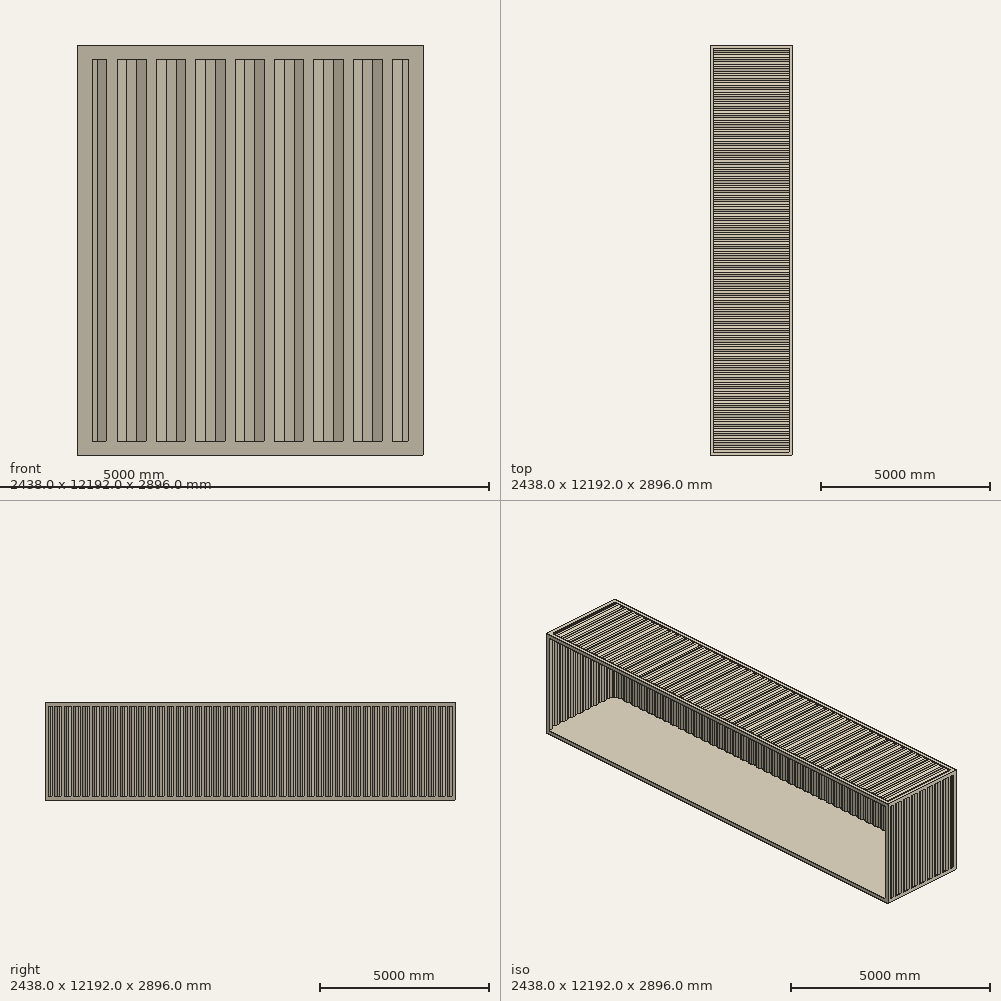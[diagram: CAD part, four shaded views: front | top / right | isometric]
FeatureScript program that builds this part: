
annotation { "Feature Type Name" : "Feature", "Feature Type Description" : "" }
export const myFeature = defineFeature(function(context is Context, id is Id, definition is map)
    precondition{}
    {
        {
            var Q0;
            Q0=qCreatedBy(makeId("Top.planeOp"),FACE);
            var sketch = newSketch(context, id + "F0", { "sketchPlane" : qUnion([Q0])});
            skLineSegment(sketch, "E0.bottom", {"start": v(0, 0) * mm, "end": v(-2438, 0) * mm});
            skLineSegment(sketch, "E0.top", {"start": v(0, 12192) * mm, "end": v(-2438, 12192) * mm});
            skLineSegment(sketch, "E0.left", {"start": v(0, 0) * mm, "end": v(0, 12192) * mm});
            skLineSegment(sketch, "E0.right", {"start": v(-2438, 0) * mm, "end": v(-2438, 12192) * mm});
            skSolve(sketch);
        }
        {
            var Q0;
            Q0=qSketchRegion(id+"F0",true);
            extrude(context, id + "F1", {"entities" : qUnion([Q0]), "depth" : 2896 * mm, "offsetDistance" : 25 * mm});
        }
        {
            var Q0;
            Q0=makeQuery(id+"F1.opExtrude","SWEPT_FACE",FACE,{"disambiguationData":[OSD([sQuery(id+"F0.wireOp",EDGE,"E0.bottom")])]});
            var sketch = newSketch(context, id + "F2", { "sketchPlane" : qUnion([Q0])});
            skLineSegment(sketch, "E1", {"start": v(-2438, 2896) * mm, "end": v(-2338, 2896) * mm});
            skLineSegment(sketch, "E2", {"start": v(-2338, 2896) * mm, "end": v(-2338, 100) * mm});
            skLineSegment(sketch, "E3", {"start": v(-2338, 100) * mm, "end": v(-100, 100) * mm});
            skLineSegment(sketch, "E4", {"start": v(-100, 100) * mm, "end": v(-100, 2796) * mm});
            skLineSegment(sketch, "E5", {"start": v(-100, 2796) * mm, "end": v(-2338, 2796) * mm});
            skSolve(sketch);
        }
        {
            var Q0;
            Q0=qSketchRegion(id+"F2",true);
            extrude(context, id + "F3", {"entities" : qUnion([Q0]), "operationType" : NewBodyOperationType.REMOVE, "oppositeDirection" : true, "depth" : 12192 * mm, "offsetDistance" : 25 * mm});
        }
        {
            var Q0;
            Q0=makeQuery(id+"F1.opExtrude","SWEPT_FACE",FACE,{"disambiguationData":[OSD([sQuery(id+"F0.wireOp",EDGE,"E0.left")])]});
            var sketch = newSketch(context, id + "F4", { "sketchPlane" : qUnion([Q0])});
            skLineSegment(sketch, "E6", {"start": v(0, 2896) * mm, "end": v(100, 2896) * mm});
            skLineSegment(sketch, "E7", {"start": v(100, 2896) * mm, "end": v(100, 100) * mm});
            skLineSegment(sketch, "E8", {"start": v(100, 100) * mm, "end": v(12092, 100) * mm});
            skLineSegment(sketch, "E9", {"start": v(12092, 100) * mm, "end": v(12092, 2796) * mm});
            skLineSegment(sketch, "E10", {"start": v(12092, 2796) * mm, "end": v(100, 2796) * mm});
            skSolve(sketch);
        }
        {
            var Q0;
            Q0=qSketchRegion(id+"F4",true);
            extrude(context, id + "F5", {"entities" : qUnion([Q0]), "operationType" : NewBodyOperationType.REMOVE, "oppositeDirection" : true, "depth" : 2438 * mm, "offsetDistance" : 25 * mm});
        }
        {
            var Q0;
            Q0=makeQuery(id+"F1.opExtrude","CAP_FACE",FACE,{"disambiguationData":[OSD([sQuery(id+"F0.wireOp",EDGE,"E0.bottom"),sQuery(id+"F0.wireOp",EDGE,"E0.top"),sQuery(id+"F0.wireOp",EDGE,"E0.left"),sQuery(id+"F0.wireOp",EDGE,"E0.right")])],"isStart":false});
            var sketch = newSketch(context, id + "F6", { "sketchPlane" : qUnion([Q0])});
            skLineSegment(sketch, "E11", {"start": v(-2438, 0) * mm, "end": v(-2338, 0) * mm});
            skLineSegment(sketch, "E12", {"start": v(-2338, 0) * mm, "end": v(-2338, 12092) * mm});
            skLineSegment(sketch, "E13", {"start": v(-2338, 12092) * mm, "end": v(-100, 12092) * mm});
            skLineSegment(sketch, "E14", {"start": v(-100, 12092) * mm, "end": v(-100, 100) * mm});
            skLineSegment(sketch, "E15", {"start": v(-100, 100) * mm, "end": v(-2338, 100) * mm});
            skSolve(sketch);
        }
        {
            var Q0;
            Q0=qSketchRegion(id+"F6",true);
            extrude(context, id + "F7", {"entities" : qUnion([Q0]), "operationType" : NewBodyOperationType.REMOVE, "oppositeDirection" : true, "depth" : 100 * mm, "offsetDistance" : 25 * mm});
        }
        {
            var Q0;
            Q0=makeQuery(id+"F5.boolean.opBoolean","MERGE",FACE,{"derivedFrom":[makeQuery(id+"F3.boolean.opBoolean","COPY",FACE,{"derivedFrom":makeQuery(id+"F3.opExtrude","SWEPT_FACE",FACE,{"disambiguationData":[OSD([sQuery(id+"F2.wireOp",EDGE,"E3")])]})})],"fromTools":[makeQuery(id+"F5.opExtrude","SWEPT_FACE",FACE,{"disambiguationData":[OSD([sQuery(id+"F4.wireOp",EDGE,"E8")])]})]});
            var sketch = newSketch(context, id + "F8", { "sketchPlane" : qUnion([Q0])});
            skLineSegment(sketch, "E16", {"start": v(-2338, 36) * mm, "end": v(-2301, 36) * mm});
            skLineSegment(sketch, "E17", {"start": v(-2233, 0) * mm, "end": v(-2161, 0) * mm});
            skLineSegment(sketch, "E18", {"start": v(-2093, 36) * mm, "end": v(-2023, 36) * mm});
            skLineSegment(sketch, "E19", {"start": v(-2301, 36) * mm, "end": v(-2233, 0) * mm});
            skLineSegment(sketch, "E20", {"start": v(-2161, 0) * mm, "end": v(-2093, 36) * mm});
            skLineSegment(sketch, "E21.1.0.0", {"start": v(-2023, 36) * mm, "end": v(-1955, 0) * mm});
            skLineSegment(sketch, "E21.1.0.1", {"start": v(-1955, 0) * mm, "end": v(-1883, 0) * mm});
            skLineSegment(sketch, "E21.1.0.2", {"start": v(-1883, 0) * mm, "end": v(-1815, 36) * mm});
            skLineSegment(sketch, "E21.1.0.3", {"start": v(-1815, 36) * mm, "end": v(-1745, 36) * mm});
            skLineSegment(sketch, "E21.2.0.0", {"start": v(-1745, 36) * mm, "end": v(-1677, 0) * mm});
            skLineSegment(sketch, "E21.2.0.1", {"start": v(-1677, 0) * mm, "end": v(-1605, 0) * mm});
            skLineSegment(sketch, "E21.2.0.2", {"start": v(-1605, 0) * mm, "end": v(-1537, 36) * mm});
            skLineSegment(sketch, "E21.2.0.3", {"start": v(-1537, 36) * mm, "end": v(-1467, 36) * mm});
            skLineSegment(sketch, "E21.3.0.0", {"start": v(-1467, 36) * mm, "end": v(-1399, 0) * mm});
            skLineSegment(sketch, "E21.3.0.1", {"start": v(-1399, 0) * mm, "end": v(-1327, 0) * mm});
            skLineSegment(sketch, "E21.3.0.2", {"start": v(-1327, 0) * mm, "end": v(-1259, 36) * mm});
            skLineSegment(sketch, "E21.3.0.3", {"start": v(-1259, 36) * mm, "end": v(-1189, 36) * mm});
            skLineSegment(sketch, "E21.4.0.0", {"start": v(-1189, 36) * mm, "end": v(-1121, 0) * mm});
            skLineSegment(sketch, "E21.4.0.1", {"start": v(-1121, 0) * mm, "end": v(-1049, 0) * mm});
            skLineSegment(sketch, "E21.4.0.2", {"start": v(-1049, 0) * mm, "end": v(-981, 36) * mm});
            skLineSegment(sketch, "E21.4.0.3", {"start": v(-981, 36) * mm, "end": v(-911, 36) * mm});
            skLineSegment(sketch, "E21.5.0.0", {"start": v(-911, 36) * mm, "end": v(-843, 0) * mm});
            skLineSegment(sketch, "E21.5.0.1", {"start": v(-843, 0) * mm, "end": v(-771, 0) * mm});
            skLineSegment(sketch, "E21.5.0.2", {"start": v(-771, 0) * mm, "end": v(-703, 36) * mm});
            skLineSegment(sketch, "E21.5.0.3", {"start": v(-703, 36) * mm, "end": v(-633, 36) * mm});
            skLineSegment(sketch, "E21.6.0.0", {"start": v(-633, 36) * mm, "end": v(-565, 0) * mm});
            skLineSegment(sketch, "E21.6.0.1", {"start": v(-565, 0) * mm, "end": v(-493, 0) * mm});
            skLineSegment(sketch, "E21.6.0.2", {"start": v(-493, 0) * mm, "end": v(-425, 36) * mm});
            skLineSegment(sketch, "E21.6.0.3", {"start": v(-425, 36) * mm, "end": v(-355, 36) * mm});
            skLineSegment(sketch, "E21.direction1", {"start": v(-2301, 36) * mm, "end": v(-2023, 36) * mm, "construction": true});
            skLineSegment(sketch, "E22.1.0.0", {"start": v(-355, 36) * mm, "end": v(-287, 0) * mm});
            skLineSegment(sketch, "E22.1.0.1", {"start": v(-287, 0) * mm, "end": v(-215, 0) * mm});
            skLineSegment(sketch, "E22.1.0.2", {"start": v(-215, 0) * mm, "end": v(-147, 36) * mm});
            skLineSegment(sketch, "E22.direction1", {"start": v(-633, 36) * mm, "end": v(-355, 36) * mm, "construction": true});
            skLineSegment(sketch, "E23", {"start": v(-147, 36) * mm, "end": v(-100, 36) * mm});
            skLineSegment(sketch, "E24.0.1.0", {"start": v(-2301, 37) * mm, "end": v(-2023, 37) * mm, "construction": true});
            skLineSegment(sketch, "E24.0.1.1", {"start": v(-633, 37) * mm, "end": v(-355, 37) * mm, "construction": true});
            skLineSegment(sketch, "E24.0.1.2", {"start": v(-355, 37) * mm, "end": v(-287, 1) * mm});
            skLineSegment(sketch, "E24.0.1.3", {"start": v(-1259, 37) * mm, "end": v(-1189, 37) * mm});
            skLineSegment(sketch, "E24.0.1.4", {"start": v(-147, 37) * mm, "end": v(-100, 37) * mm});
            skLineSegment(sketch, "E24.0.1.5", {"start": v(-1605, 1) * mm, "end": v(-1537, 37) * mm});
            skLineSegment(sketch, "E24.0.1.6", {"start": v(-1467, 37) * mm, "end": v(-1399, 1) * mm});
            skLineSegment(sketch, "E24.0.1.7", {"start": v(-1049, 1) * mm, "end": v(-981, 37) * mm});
            skLineSegment(sketch, "E24.0.1.8", {"start": v(-633, 37) * mm, "end": v(-565, 1) * mm});
            skLineSegment(sketch, "E24.0.1.9", {"start": v(-1955, 1) * mm, "end": v(-1883, 1) * mm});
            skLineSegment(sketch, "E24.0.1.10", {"start": v(-215, 1) * mm, "end": v(-147, 37) * mm});
            skLineSegment(sketch, "E24.0.1.11", {"start": v(-911, 37) * mm, "end": v(-843, 1) * mm});
            skLineSegment(sketch, "E24.0.1.12", {"start": v(-1883, 1) * mm, "end": v(-1815, 37) * mm});
            skLineSegment(sketch, "E24.0.1.13", {"start": v(-2023, 37) * mm, "end": v(-1955, 1) * mm});
            skLineSegment(sketch, "E24.0.1.14", {"start": v(-493, 1) * mm, "end": v(-425, 37) * mm});
            skLineSegment(sketch, "E24.0.1.15", {"start": v(-1677, 1) * mm, "end": v(-1605, 1) * mm});
            skLineSegment(sketch, "E24.0.1.16", {"start": v(-1189, 37) * mm, "end": v(-1121, 1) * mm});
            skLineSegment(sketch, "E24.0.1.17", {"start": v(-1745, 37) * mm, "end": v(-1677, 1) * mm});
            skLineSegment(sketch, "E24.0.1.18", {"start": v(-287, 1) * mm, "end": v(-215, 1) * mm});
            skLineSegment(sketch, "E24.0.1.19", {"start": v(-981, 37) * mm, "end": v(-911, 37) * mm});
            skLineSegment(sketch, "E24.0.1.20", {"start": v(-843, 1) * mm, "end": v(-771, 1) * mm});
            skLineSegment(sketch, "E24.0.1.21", {"start": v(-771, 1) * mm, "end": v(-703, 37) * mm});
            skLineSegment(sketch, "E24.0.1.22", {"start": v(-1815, 37) * mm, "end": v(-1745, 37) * mm});
            skLineSegment(sketch, "E24.0.1.23", {"start": v(-565, 1) * mm, "end": v(-493, 1) * mm});
            skLineSegment(sketch, "E24.0.1.24", {"start": v(-2161, 1) * mm, "end": v(-2093, 37) * mm});
            skLineSegment(sketch, "E24.0.1.25", {"start": v(-1121, 1) * mm, "end": v(-1049, 1) * mm});
            skLineSegment(sketch, "E24.0.1.26", {"start": v(-2301, 37) * mm, "end": v(-2233, 1) * mm});
            skLineSegment(sketch, "E24.0.1.27", {"start": v(-1537, 37) * mm, "end": v(-1467, 37) * mm});
            skLineSegment(sketch, "E24.0.1.28", {"start": v(-1399, 1) * mm, "end": v(-1327, 1) * mm});
            skLineSegment(sketch, "E24.0.1.29", {"start": v(-2233, 1) * mm, "end": v(-2161, 1) * mm});
            skLineSegment(sketch, "E24.0.1.30", {"start": v(-1327, 1) * mm, "end": v(-1259, 37) * mm});
            skLineSegment(sketch, "E24.0.1.31", {"start": v(-425, 37) * mm, "end": v(-355, 37) * mm});
            skLineSegment(sketch, "E24.0.1.32", {"start": v(-2093, 37) * mm, "end": v(-2023, 37) * mm});
            skLineSegment(sketch, "E24.0.1.33", {"start": v(-703, 37) * mm, "end": v(-633, 37) * mm});
            skLineSegment(sketch, "E24.0.1.34", {"start": v(-2338, 37) * mm, "end": v(-2301, 37) * mm});
            skLineSegment(sketch, "E24.direction1", {"start": v(-2338, 36) * mm, "end": v(-2313, 36) * mm, "construction": true});
            skLineSegment(sketch, "E24.direction2", {"start": v(-2338, 36) * mm, "end": v(-2338, 37) * mm, "construction": true});
            skLineSegment(sketch, "E25", {"start": v(-2338, 37) * mm, "end": v(-2338, 36) * mm});
            skLineSegment(sketch, "E26", {"start": v(-100, 37) * mm, "end": v(-100, 36) * mm});
            skSolve(sketch);
        }
        {
            var Q0;
            Q0=qSketchRegion(id+"F8",true);
            extrude(context, id + "F9", {"entities" : qUnion([Q0]), "operationType" : NewBodyOperationType.ADD, "depth" : 2696 * mm, "offsetDistance" : 25 * mm});
        }
        {
            var Q0;
            {var subQ4=makeQuery(id+"F3.boolean.opBoolean","COPY",FACE,{"derivedFrom":makeQuery(id+"F3.opExtrude","SWEPT_FACE",FACE,{"disambiguationData":[OSD([sQuery(id+"F2.wireOp",EDGE,"E3")])]})});var subQ5=makeQuery(id+"F5.opExtrude","SWEPT_FACE",FACE,{"disambiguationData":[OSD([sQuery(id+"F4.wireOp",EDGE,"E8")])]});Q0=makeQuery(id+"F9.boolean.opBoolean","SPLIT",FACE,{"disambiguationData":[TD([makeQuery(id+"F1.opExtrude","SWEPT_FACE",FACE,{"disambiguationData":[OSD([sQuery(id+"F0.wireOp",EDGE,"E0.top")])]})])],"derivedFrom":makeQuery(id+"F5.boolean.opBoolean","MERGE",FACE,{"derivedFrom":[subQ4],"fromTools":[subQ5]})});}
            var sketch = newSketch(context, id + "F10", { "sketchPlane" : qUnion([Q0])});
            skLineSegment(sketch, "E27", {"start": v(-100, 12156) * mm, "end": v(-137, 12156) * mm});
            skLineSegment(sketch, "E28", {"start": v(-205.08, 12191.96) * mm, "end": v(-277.08, 12191.96) * mm});
            skLineSegment(sketch, "E29", {"start": v(-345, 12156) * mm, "end": v(-415, 12156) * mm});
            skLineSegment(sketch, "E30", {"start": v(-137, 12156) * mm, "end": v(-205.08, 12191.96) * mm});
            skLineSegment(sketch, "E31", {"start": v(-277.08, 12191.96) * mm, "end": v(-345, 12156) * mm});
            skLineSegment(sketch, "E32.1.0.0", {"start": v(-415, 12156) * mm, "end": v(-483.08, 12191.96) * mm});
            skLineSegment(sketch, "E32.1.0.1", {"start": v(-483.08, 12191.96) * mm, "end": v(-555.08, 12191.96) * mm});
            skLineSegment(sketch, "E32.1.0.2", {"start": v(-555.08, 12191.96) * mm, "end": v(-623, 12156) * mm});
            skLineSegment(sketch, "E32.1.0.3", {"start": v(-623, 12156) * mm, "end": v(-693, 12156) * mm});
            skLineSegment(sketch, "E32.2.0.0", {"start": v(-693, 12156) * mm, "end": v(-761.08, 12191.96) * mm});
            skLineSegment(sketch, "E32.2.0.1", {"start": v(-761.08, 12191.96) * mm, "end": v(-833.08, 12191.96) * mm});
            skLineSegment(sketch, "E32.2.0.2", {"start": v(-833.08, 12191.96) * mm, "end": v(-901, 12156) * mm});
            skLineSegment(sketch, "E32.2.0.3", {"start": v(-901, 12156) * mm, "end": v(-971, 12156) * mm});
            skLineSegment(sketch, "E32.3.0.0", {"start": v(-971, 12156) * mm, "end": v(-1039.08, 12191.96) * mm});
            skLineSegment(sketch, "E32.3.0.1", {"start": v(-1039.08, 12191.96) * mm, "end": v(-1111.08, 12191.96) * mm});
            skLineSegment(sketch, "E32.3.0.2", {"start": v(-1111.08, 12191.96) * mm, "end": v(-1179, 12156) * mm});
            skLineSegment(sketch, "E32.3.0.3", {"start": v(-1179, 12156) * mm, "end": v(-1249, 12156) * mm});
            skLineSegment(sketch, "E32.4.0.0", {"start": v(-1249, 12156) * mm, "end": v(-1317.08, 12191.96) * mm});
            skLineSegment(sketch, "E32.4.0.1", {"start": v(-1317.08, 12191.96) * mm, "end": v(-1389.08, 12191.96) * mm});
            skLineSegment(sketch, "E32.4.0.2", {"start": v(-1389.08, 12191.96) * mm, "end": v(-1457, 12156) * mm});
            skLineSegment(sketch, "E32.4.0.3", {"start": v(-1457, 12156) * mm, "end": v(-1527, 12156) * mm});
            skLineSegment(sketch, "E32.5.0.0", {"start": v(-1527, 12156) * mm, "end": v(-1595.08, 12191.96) * mm});
            skLineSegment(sketch, "E32.5.0.1", {"start": v(-1595.08, 12191.96) * mm, "end": v(-1667.08, 12191.96) * mm});
            skLineSegment(sketch, "E32.5.0.2", {"start": v(-1667.08, 12191.96) * mm, "end": v(-1735, 12156) * mm});
            skLineSegment(sketch, "E32.5.0.3", {"start": v(-1735, 12156) * mm, "end": v(-1805, 12156) * mm});
            skLineSegment(sketch, "E32.6.0.0", {"start": v(-1805, 12156) * mm, "end": v(-1873.08, 12191.96) * mm});
            skLineSegment(sketch, "E32.6.0.1", {"start": v(-1873.08, 12191.96) * mm, "end": v(-1945.08, 12191.96) * mm});
            skLineSegment(sketch, "E32.6.0.2", {"start": v(-1945.08, 12191.96) * mm, "end": v(-2013, 12156) * mm});
            skLineSegment(sketch, "E32.6.0.3", {"start": v(-2013, 12156) * mm, "end": v(-2083, 12156) * mm});
            skLineSegment(sketch, "E32.direction1", {"start": v(-137, 12156) * mm, "end": v(-415, 12156) * mm, "construction": true});
            skLineSegment(sketch, "E33.1.0.0", {"start": v(-2083, 12156) * mm, "end": v(-2151.08, 12191.96) * mm});
            skLineSegment(sketch, "E33.1.0.1", {"start": v(-2151.08, 12191.96) * mm, "end": v(-2223.08, 12191.96) * mm});
            skLineSegment(sketch, "E33.1.0.2", {"start": v(-2223.08, 12191.96) * mm, "end": v(-2291, 12156) * mm});
            skLineSegment(sketch, "E33.direction1", {"start": v(-1805, 12156) * mm, "end": v(-2083, 12156) * mm, "construction": true});
            skLineSegment(sketch, "E34", {"start": v(-2291, 12156) * mm, "end": v(-2338, 12156) * mm});
            skLineSegment(sketch, "E35.0.1.0", {"start": v(-137, 12155) * mm, "end": v(-415, 12155) * mm, "construction": true});
            skLineSegment(sketch, "E35.0.1.1", {"start": v(-1805, 12155) * mm, "end": v(-2083, 12155) * mm, "construction": true});
            skLineSegment(sketch, "E35.0.1.2", {"start": v(-2083, 12155) * mm, "end": v(-2151.08, 12190.96) * mm});
            skLineSegment(sketch, "E35.0.1.3", {"start": v(-1179, 12155) * mm, "end": v(-1249, 12155) * mm});
            skLineSegment(sketch, "E35.0.1.4", {"start": v(-2291, 12155) * mm, "end": v(-2338, 12155) * mm});
            skLineSegment(sketch, "E35.0.1.5", {"start": v(-833.08, 12190.96) * mm, "end": v(-901, 12155) * mm});
            skLineSegment(sketch, "E35.0.1.6", {"start": v(-971, 12155) * mm, "end": v(-1039.08, 12190.96) * mm});
            skLineSegment(sketch, "E35.0.1.7", {"start": v(-1389.08, 12190.96) * mm, "end": v(-1457, 12155) * mm});
            skLineSegment(sketch, "E35.0.1.8", {"start": v(-1805, 12155) * mm, "end": v(-1873.08, 12190.96) * mm});
            skLineSegment(sketch, "E35.0.1.9", {"start": v(-483.08, 12190.96) * mm, "end": v(-555.08, 12190.96) * mm});
            skLineSegment(sketch, "E35.0.1.10", {"start": v(-2223.08, 12190.96) * mm, "end": v(-2291, 12155) * mm});
            skLineSegment(sketch, "E35.0.1.11", {"start": v(-1527, 12155) * mm, "end": v(-1595.08, 12190.96) * mm});
            skLineSegment(sketch, "E35.0.1.12", {"start": v(-555.08, 12190.96) * mm, "end": v(-623, 12155) * mm});
            skLineSegment(sketch, "E35.0.1.13", {"start": v(-415, 12155) * mm, "end": v(-483.08, 12190.96) * mm});
            skLineSegment(sketch, "E35.0.1.14", {"start": v(-1945.08, 12190.96) * mm, "end": v(-2013, 12155) * mm});
            skLineSegment(sketch, "E35.0.1.15", {"start": v(-761.08, 12190.96) * mm, "end": v(-833.08, 12190.96) * mm});
            skLineSegment(sketch, "E35.0.1.16", {"start": v(-1249, 12155) * mm, "end": v(-1317.08, 12190.96) * mm});
            skLineSegment(sketch, "E35.0.1.17", {"start": v(-693, 12155) * mm, "end": v(-761.08, 12190.96) * mm});
            skLineSegment(sketch, "E35.0.1.18", {"start": v(-2151.08, 12190.96) * mm, "end": v(-2223.08, 12190.96) * mm});
            skLineSegment(sketch, "E35.0.1.19", {"start": v(-1457, 12155) * mm, "end": v(-1527, 12155) * mm});
            skLineSegment(sketch, "E35.0.1.20", {"start": v(-1595.08, 12190.96) * mm, "end": v(-1667.08, 12190.96) * mm});
            skLineSegment(sketch, "E35.0.1.21", {"start": v(-1667.08, 12190.96) * mm, "end": v(-1735, 12155) * mm});
            skLineSegment(sketch, "E35.0.1.22", {"start": v(-623, 12155) * mm, "end": v(-693, 12155) * mm});
            skLineSegment(sketch, "E35.0.1.23", {"start": v(-1873.08, 12190.96) * mm, "end": v(-1945.08, 12190.96) * mm});
            skLineSegment(sketch, "E35.0.1.24", {"start": v(-277.08, 12190.96) * mm, "end": v(-345, 12155) * mm});
            skLineSegment(sketch, "E35.0.1.25", {"start": v(-1317.08, 12190.96) * mm, "end": v(-1389.08, 12190.96) * mm});
            skLineSegment(sketch, "E35.0.1.26", {"start": v(-137, 12155) * mm, "end": v(-205.08, 12190.96) * mm});
            skLineSegment(sketch, "E35.0.1.27", {"start": v(-901, 12155) * mm, "end": v(-971, 12155) * mm});
            skLineSegment(sketch, "E35.0.1.28", {"start": v(-1039.08, 12190.96) * mm, "end": v(-1111.08, 12190.96) * mm});
            skLineSegment(sketch, "E35.0.1.29", {"start": v(-205.08, 12190.96) * mm, "end": v(-277.08, 12190.96) * mm});
            skLineSegment(sketch, "E35.0.1.30", {"start": v(-1111.08, 12190.96) * mm, "end": v(-1179, 12155) * mm});
            skLineSegment(sketch, "E35.0.1.31", {"start": v(-2013, 12155) * mm, "end": v(-2083, 12155) * mm});
            skLineSegment(sketch, "E35.0.1.32", {"start": v(-345, 12155) * mm, "end": v(-415, 12155) * mm});
            skLineSegment(sketch, "E35.0.1.33", {"start": v(-1735, 12155) * mm, "end": v(-1805, 12155) * mm});
            skLineSegment(sketch, "E35.0.1.34", {"start": v(-100, 12155) * mm, "end": v(-137, 12155) * mm});
            skLineSegment(sketch, "E35.direction1", {"start": v(-100, 12156) * mm, "end": v(-125, 12156) * mm, "construction": true});
            skLineSegment(sketch, "E35.direction2", {"start": v(-100, 12156) * mm, "end": v(-100, 12155) * mm, "construction": true});
            skLineSegment(sketch, "E36", {"start": v(-100, 12156) * mm, "end": v(-100, 12155) * mm});
            skLineSegment(sketch, "E37", {"start": v(-2338, 12156) * mm, "end": v(-2338, 12155) * mm});
            skSolve(sketch);
        }
        {
            var Q0;
            Q0=qSketchRegion(id+"F10",true);
            extrude(context, id + "F11", {"entities" : qUnion([Q0]), "operationType" : NewBodyOperationType.ADD, "depth" : 2696 * mm, "offsetDistance" : 25 * mm});
        }
        {
            var Q0;
            {var subQ5=makeQuery(id+"F3.boolean.opBoolean","COPY",FACE,{"derivedFrom":makeQuery(id+"F3.opExtrude","SWEPT_FACE",FACE,{"disambiguationData":[OSD([sQuery(id+"F2.wireOp",EDGE,"E3")])]})});var subQ6=makeQuery(id+"F5.opExtrude","SWEPT_FACE",FACE,{"disambiguationData":[OSD([sQuery(id+"F4.wireOp",EDGE,"E8")])]});var subQ12=makeQuery(id+"F1.opExtrude","SWEPT_FACE",FACE,{"disambiguationData":[OSD([sQuery(id+"F0.wireOp",EDGE,"E0.left")])]});Q0=makeQuery(id+"F11.boolean.opBoolean","SPLIT",FACE,{"disambiguationData":[TD([subQ12])],"derivedFrom":makeQuery(id+"F9.boolean.opBoolean","SPLIT",FACE,{"disambiguationData":[TD([makeQuery(id+"F1.opExtrude","SWEPT_FACE",FACE,{"disambiguationData":[OSD([sQuery(id+"F0.wireOp",EDGE,"E0.top")])]})])],"derivedFrom":makeQuery(id+"F5.boolean.opBoolean","MERGE",FACE,{"derivedFrom":[subQ5],"fromTools":[subQ6]})})});}
            var sketch = newSketch(context, id + "F12", { "sketchPlane" : qUnion([Q0])});
            skLineSegment(sketch, "E38", {"start": v(0, 100) * mm, "end": v(-36, 100) * mm});
            skLineSegment(sketch, "E39", {"start": v(-36, 100.17) * mm, "end": v(-36, 137.17) * mm});
            skLineSegment(sketch, "E40", {"start": v(0, 205.17) * mm, "end": v(0, 277.17) * mm});
            skLineSegment(sketch, "E41", {"start": v(-36, 345.17) * mm, "end": v(-36, 415.17) * mm});
            skLineSegment(sketch, "E42", {"start": v(-36, 137.17) * mm, "end": v(0, 205.17) * mm});
            skLineSegment(sketch, "E43", {"start": v(0, 277.17) * mm, "end": v(-36, 345.17) * mm});
            skLineSegment(sketch, "E44.1.0.0", {"start": v(-36, 415.17) * mm, "end": v(0, 483.17) * mm});
            skLineSegment(sketch, "E44.1.0.1", {"start": v(0, 483.17) * mm, "end": v(0, 555.17) * mm});
            skLineSegment(sketch, "E44.1.0.2", {"start": v(0, 555.17) * mm, "end": v(-36, 623.17) * mm});
            skLineSegment(sketch, "E44.1.0.3", {"start": v(-36, 623.17) * mm, "end": v(-36, 693.17) * mm});
            skLineSegment(sketch, "E44.2.0.0", {"start": v(-36, 693.17) * mm, "end": v(0, 761.17) * mm});
            skLineSegment(sketch, "E44.2.0.1", {"start": v(0, 761.17) * mm, "end": v(0, 833.17) * mm});
            skLineSegment(sketch, "E44.2.0.2", {"start": v(0, 833.17) * mm, "end": v(-36, 901.17) * mm});
            skLineSegment(sketch, "E44.2.0.3", {"start": v(-36, 901.17) * mm, "end": v(-36, 971.17) * mm});
            skLineSegment(sketch, "E44.3.0.0", {"start": v(-36, 971.17) * mm, "end": v(0, 1039.17) * mm});
            skLineSegment(sketch, "E44.3.0.1", {"start": v(0, 1039.17) * mm, "end": v(0, 1111.17) * mm});
            skLineSegment(sketch, "E44.3.0.2", {"start": v(0, 1111.17) * mm, "end": v(-36, 1179.17) * mm});
            skLineSegment(sketch, "E44.3.0.3", {"start": v(-36, 1179.17) * mm, "end": v(-36, 1249.17) * mm});
            skLineSegment(sketch, "E44.4.0.0", {"start": v(-36, 1249.17) * mm, "end": v(0, 1317.17) * mm});
            skLineSegment(sketch, "E44.4.0.1", {"start": v(0, 1317.17) * mm, "end": v(0, 1389.17) * mm});
            skLineSegment(sketch, "E44.4.0.2", {"start": v(0, 1389.17) * mm, "end": v(-36, 1457.17) * mm});
            skLineSegment(sketch, "E44.4.0.3", {"start": v(-36, 1457.17) * mm, "end": v(-36, 1527.17) * mm});
            skLineSegment(sketch, "E44.5.0.0", {"start": v(-36, 1527.17) * mm, "end": v(0, 1595.17) * mm});
            skLineSegment(sketch, "E44.5.0.1", {"start": v(0, 1595.17) * mm, "end": v(0, 1667.17) * mm});
            skLineSegment(sketch, "E44.5.0.2", {"start": v(0, 1667.17) * mm, "end": v(-36, 1735.17) * mm});
            skLineSegment(sketch, "E44.5.0.3", {"start": v(-36, 1735.17) * mm, "end": v(-36, 1805.17) * mm});
            skLineSegment(sketch, "E44.6.0.0", {"start": v(-36, 1805.17) * mm, "end": v(0, 1873.17) * mm});
            skLineSegment(sketch, "E44.6.0.1", {"start": v(0, 1873.17) * mm, "end": v(0, 1945.17) * mm});
            skLineSegment(sketch, "E44.6.0.2", {"start": v(0, 1945.17) * mm, "end": v(-36, 2013.17) * mm});
            skLineSegment(sketch, "E44.6.0.3", {"start": v(-36, 2013.17) * mm, "end": v(-36, 2083.17) * mm});
            skLineSegment(sketch, "E44.direction1", {"start": v(-36, 137.17) * mm, "end": v(-36, 415.17) * mm, "construction": true});
            skLineSegment(sketch, "E45.1.0.0", {"start": v(-36, 2083.17) * mm, "end": v(0, 2151.17) * mm});
            skLineSegment(sketch, "E45.1.0.1", {"start": v(0, 2151.17) * mm, "end": v(0, 2223.17) * mm});
            skLineSegment(sketch, "E45.1.0.2", {"start": v(0, 2223.17) * mm, "end": v(-36, 2291.17) * mm});
            skLineSegment(sketch, "E45.direction1", {"start": v(-36, 1805.17) * mm, "end": v(-36, 2083.17) * mm, "construction": true});
            skLineSegment(sketch, "E46.0.1.0", {"start": v(-37, 137.17) * mm, "end": v(-37, 415.17) * mm, "construction": true});
            skLineSegment(sketch, "E46.0.1.1", {"start": v(-37, 1805.17) * mm, "end": v(-37, 2083.17) * mm, "construction": true});
            skLineSegment(sketch, "E46.0.1.2", {"start": v(-37, 2083.17) * mm, "end": v(-1, 2151.17) * mm});
            skLineSegment(sketch, "E46.0.1.3", {"start": v(-37, 1179.17) * mm, "end": v(-37, 1249.17) * mm});
            skLineSegment(sketch, "E46.0.1.5", {"start": v(-1, 833.17) * mm, "end": v(-37, 901.17) * mm});
            skLineSegment(sketch, "E46.0.1.6", {"start": v(-37, 971.17) * mm, "end": v(-1, 1039.17) * mm});
            skLineSegment(sketch, "E46.0.1.7", {"start": v(-1, 1389.17) * mm, "end": v(-37, 1457.17) * mm});
            skLineSegment(sketch, "E46.0.1.8", {"start": v(-37, 1805.17) * mm, "end": v(-1, 1873.17) * mm});
            skLineSegment(sketch, "E46.0.1.9", {"start": v(-1, 483.17) * mm, "end": v(-1, 555.17) * mm});
            skLineSegment(sketch, "E46.0.1.10", {"start": v(-1, 2223.17) * mm, "end": v(-37, 2291.17) * mm});
            skLineSegment(sketch, "E46.0.1.11", {"start": v(-37, 1527.17) * mm, "end": v(-1, 1595.17) * mm});
            skLineSegment(sketch, "E46.0.1.12", {"start": v(-1, 555.17) * mm, "end": v(-37, 623.17) * mm});
            skLineSegment(sketch, "E46.0.1.13", {"start": v(-37, 415.17) * mm, "end": v(-1, 483.17) * mm});
            skLineSegment(sketch, "E46.0.1.14", {"start": v(-1, 1945.17) * mm, "end": v(-37, 2013.17) * mm});
            skLineSegment(sketch, "E46.0.1.15", {"start": v(-1, 761.17) * mm, "end": v(-1, 833.17) * mm});
            skLineSegment(sketch, "E46.0.1.16", {"start": v(-37, 1249.17) * mm, "end": v(-1, 1317.17) * mm});
            skLineSegment(sketch, "E46.0.1.17", {"start": v(-37, 693.17) * mm, "end": v(-1, 761.17) * mm});
            skLineSegment(sketch, "E46.0.1.18", {"start": v(-1, 2151.17) * mm, "end": v(-1, 2223.17) * mm});
            skLineSegment(sketch, "E46.0.1.19", {"start": v(-37, 1457.17) * mm, "end": v(-37, 1527.17) * mm});
            skLineSegment(sketch, "E46.0.1.20", {"start": v(-1, 1595.17) * mm, "end": v(-1, 1667.17) * mm});
            skLineSegment(sketch, "E46.0.1.21", {"start": v(-1, 1667.17) * mm, "end": v(-37, 1735.17) * mm});
            skLineSegment(sketch, "E46.0.1.22", {"start": v(-37, 623.17) * mm, "end": v(-37, 693.17) * mm});
            skLineSegment(sketch, "E46.0.1.23", {"start": v(-1, 1873.17) * mm, "end": v(-1, 1945.17) * mm});
            skLineSegment(sketch, "E46.0.1.24", {"start": v(-1, 277.17) * mm, "end": v(-37, 345.17) * mm});
            skLineSegment(sketch, "E46.0.1.25", {"start": v(-1, 1317.17) * mm, "end": v(-1, 1389.17) * mm});
            skLineSegment(sketch, "E46.0.1.26", {"start": v(-37, 137.17) * mm, "end": v(-1, 205.17) * mm});
            skLineSegment(sketch, "E46.0.1.27", {"start": v(-37, 901.17) * mm, "end": v(-37, 971.17) * mm});
            skLineSegment(sketch, "E46.0.1.28", {"start": v(-1, 1039.17) * mm, "end": v(-1, 1111.17) * mm});
            skLineSegment(sketch, "E46.0.1.29", {"start": v(-1, 205.17) * mm, "end": v(-1, 277.17) * mm});
            skLineSegment(sketch, "E46.0.1.30", {"start": v(-1, 1111.17) * mm, "end": v(-37, 1179.17) * mm});
            skLineSegment(sketch, "E46.0.1.31", {"start": v(-37, 2013.17) * mm, "end": v(-37, 2083.17) * mm});
            skLineSegment(sketch, "E46.0.1.32", {"start": v(-37, 345.17) * mm, "end": v(-37, 415.17) * mm});
            skLineSegment(sketch, "E46.0.1.33", {"start": v(-37, 1735.17) * mm, "end": v(-37, 1805.17) * mm});
            skLineSegment(sketch, "E46.0.1.34", {"start": v(-37, 100.17) * mm, "end": v(-37, 137.17) * mm});
            skLineSegment(sketch, "E47", {"start": v(-37, 100.17) * mm, "end": v(-37, 100) * mm});
            skLineSegment(sketch, "E48", {"start": v(-37, 100) * mm, "end": v(-36, 100) * mm});
            skLineSegment(sketch, "E49", {"start": v(-36, 100) * mm, "end": v(-36, 100.17) * mm});
            skLineSegment(sketch, "E50.0.1.0", {"start": v(0, 2779.17) * mm, "end": v(-36, 2847.17) * mm});
            skLineSegment(sketch, "E50.0.1.1", {"start": v(-1, 2779.17) * mm, "end": v(-37, 2847.17) * mm});
            skLineSegment(sketch, "E50.0.1.2", {"start": v(0, 2707.17) * mm, "end": v(0, 2779.17) * mm});
            skLineSegment(sketch, "E50.0.1.3", {"start": v(0, 2429.17) * mm, "end": v(0, 2501.17) * mm});
            skLineSegment(sketch, "E50.0.1.4", {"start": v(-37, 2639.17) * mm, "end": v(-1, 2707.17) * mm});
            skLineSegment(sketch, "E50.0.1.5", {"start": v(-37, 2569.17) * mm, "end": v(-37, 2639.17) * mm});
            skLineSegment(sketch, "E50.0.1.6", {"start": v(-37, 2917.17) * mm, "end": v(-1, 2985.17) * mm});
            skLineSegment(sketch, "E50.0.1.7", {"start": v(-1, 2501.17) * mm, "end": v(-37, 2569.17) * mm});
            skLineSegment(sketch, "E50.0.1.8", {"start": v(-36, 2917.17) * mm, "end": v(0, 2985.17) * mm});
            skLineSegment(sketch, "E50.0.1.9", {"start": v(-36, 2569.17) * mm, "end": v(-36, 2639.17) * mm});
            skLineSegment(sketch, "E50.0.1.10", {"start": v(-37, 2291.17) * mm, "end": v(-37, 2361.17) * mm});
            skLineSegment(sketch, "E50.0.1.11", {"start": v(-36, 2847.17) * mm, "end": v(-36, 2917.17) * mm});
            skLineSegment(sketch, "E50.0.1.12", {"start": v(-1, 2707.17) * mm, "end": v(-1, 2779.17) * mm});
            skLineSegment(sketch, "E50.0.1.13", {"start": v(-37, 2361.17) * mm, "end": v(-1, 2429.17) * mm});
            skLineSegment(sketch, "E50.0.1.14", {"start": v(-36, 2361.17) * mm, "end": v(0, 2429.17) * mm});
            skLineSegment(sketch, "E50.0.1.15", {"start": v(0, 2985.17) * mm, "end": v(0, 3057.17) * mm});
            skLineSegment(sketch, "E50.0.1.16", {"start": v(0, 2501.17) * mm, "end": v(-36, 2569.17) * mm});
            skLineSegment(sketch, "E50.0.1.17", {"start": v(-36, 2291.17) * mm, "end": v(-36, 2361.17) * mm});
            skLineSegment(sketch, "E50.0.1.18", {"start": v(-1, 2429.17) * mm, "end": v(-1, 2501.17) * mm});
            skLineSegment(sketch, "E50.0.1.19", {"start": v(-36, 2639.17) * mm, "end": v(0, 2707.17) * mm});
            skLineSegment(sketch, "E50.0.1.20", {"start": v(-1, 2985.17) * mm, "end": v(-1, 3057.17) * mm});
            skLineSegment(sketch, "E50.0.1.21", {"start": v(-37, 2847.17) * mm, "end": v(-37, 2917.17) * mm});
            skLineSegment(sketch, "E50.0.1.22", {"start": v(-36, 3751.17) * mm, "end": v(-36, 4029.17) * mm, "construction": true});
            skLineSegment(sketch, "E50.0.1.23", {"start": v(0, 4169.17) * mm, "end": v(-36, 4237.17) * mm});
            skLineSegment(sketch, "E50.0.1.24", {"start": v(-1, 4169.17) * mm, "end": v(-37, 4237.17) * mm});
            skLineSegment(sketch, "E50.0.1.25", {"start": v(-37, 3751.17) * mm, "end": v(-37, 4029.17) * mm, "construction": true});
            skLineSegment(sketch, "E50.0.1.26", {"start": v(-1, 3335.17) * mm, "end": v(-37, 3403.17) * mm});
            skLineSegment(sketch, "E50.0.1.27", {"start": v(0, 3335.17) * mm, "end": v(-36, 3403.17) * mm});
            skLineSegment(sketch, "E50.0.1.28", {"start": v(0, 4097.17) * mm, "end": v(0, 4169.17) * mm});
            skLineSegment(sketch, "E50.0.1.29", {"start": v(-36, 4029.17) * mm, "end": v(0, 4097.17) * mm});
            skLineSegment(sketch, "E50.0.1.30", {"start": v(0, 3263.17) * mm, "end": v(0, 3335.17) * mm});
            skLineSegment(sketch, "E50.0.1.31", {"start": v(-1, 3263.17) * mm, "end": v(-1, 3335.17) * mm});
            skLineSegment(sketch, "E50.0.1.32", {"start": v(-37, 4029.17) * mm, "end": v(-1, 4097.17) * mm});
            skLineSegment(sketch, "E50.0.1.33", {"start": v(-1, 4097.17) * mm, "end": v(-1, 4169.17) * mm});
            skLineSegment(sketch, "E50.0.1.34", {"start": v(-37, 3681.17) * mm, "end": v(-37, 3751.17) * mm});
            skLineSegment(sketch, "E50.0.1.35", {"start": v(-1, 3541.17) * mm, "end": v(-1, 3613.17) * mm});
            skLineSegment(sketch, "E50.0.1.36", {"start": v(-37, 3125.17) * mm, "end": v(-37, 3195.17) * mm});
            skLineSegment(sketch, "E50.0.1.37", {"start": v(-1, 3891.17) * mm, "end": v(-37, 3959.17) * mm});
            skLineSegment(sketch, "E50.0.1.38", {"start": v(-36, 3473.17) * mm, "end": v(0, 3541.17) * mm});
            skLineSegment(sketch, "E50.0.1.39", {"start": v(-1, 3613.17) * mm, "end": v(-37, 3681.17) * mm});
            skLineSegment(sketch, "E50.0.1.40", {"start": v(0, 3819.17) * mm, "end": v(0, 3891.17) * mm});
            skLineSegment(sketch, "E50.0.1.41", {"start": v(-36, 3751.17) * mm, "end": v(0, 3819.17) * mm});
            skLineSegment(sketch, "E50.0.1.42", {"start": v(0, 3541.17) * mm, "end": v(0, 3613.17) * mm});
            skLineSegment(sketch, "E50.0.1.43", {"start": v(-36, 3125.17) * mm, "end": v(-36, 3195.17) * mm});
            skLineSegment(sketch, "E50.0.1.44", {"start": v(-37, 3473.17) * mm, "end": v(-1, 3541.17) * mm});
            skLineSegment(sketch, "E50.0.1.45", {"start": v(-37, 3195.17) * mm, "end": v(-1, 3263.17) * mm});
            skLineSegment(sketch, "E50.0.1.46", {"start": v(-1, 3057.17) * mm, "end": v(-37, 3125.17) * mm});
            skLineSegment(sketch, "E50.0.1.47", {"start": v(-1, 3819.17) * mm, "end": v(-1, 3891.17) * mm});
            skLineSegment(sketch, "E50.0.1.48", {"start": v(-37, 3403.17) * mm, "end": v(-37, 3473.17) * mm});
            skLineSegment(sketch, "E50.0.1.49", {"start": v(-37, 3959.17) * mm, "end": v(-37, 4029.17) * mm});
            skLineSegment(sketch, "E50.0.1.50", {"start": v(-36, 3403.17) * mm, "end": v(-36, 3473.17) * mm});
            skLineSegment(sketch, "E50.0.1.51", {"start": v(0, 3057.17) * mm, "end": v(-36, 3125.17) * mm});
            skLineSegment(sketch, "E50.0.1.52", {"start": v(-36, 3195.17) * mm, "end": v(0, 3263.17) * mm});
            skLineSegment(sketch, "E50.0.1.53", {"start": v(-36, 3959.17) * mm, "end": v(-36, 4029.17) * mm});
            skLineSegment(sketch, "E50.0.1.54", {"start": v(-36, 3681.17) * mm, "end": v(-36, 3751.17) * mm});
            skLineSegment(sketch, "E50.0.1.55", {"start": v(0, 3891.17) * mm, "end": v(-36, 3959.17) * mm});
            skLineSegment(sketch, "E50.0.1.56", {"start": v(0, 3613.17) * mm, "end": v(-36, 3681.17) * mm});
            skLineSegment(sketch, "E50.0.1.57", {"start": v(-37, 3751.17) * mm, "end": v(-1, 3819.17) * mm});
            skLineSegment(sketch, "E50.0.2.0", {"start": v(0, 4725.17) * mm, "end": v(-36, 4793.17) * mm});
            skLineSegment(sketch, "E50.0.2.1", {"start": v(-1, 4725.17) * mm, "end": v(-37, 4793.17) * mm});
            skLineSegment(sketch, "E50.0.2.2", {"start": v(0, 4653.17) * mm, "end": v(0, 4725.17) * mm});
            skLineSegment(sketch, "E50.0.2.3", {"start": v(0, 4375.17) * mm, "end": v(0, 4447.17) * mm});
            skLineSegment(sketch, "E50.0.2.4", {"start": v(-37, 4585.17) * mm, "end": v(-1, 4653.17) * mm});
            skLineSegment(sketch, "E50.0.2.5", {"start": v(-37, 4515.17) * mm, "end": v(-37, 4585.17) * mm});
            skLineSegment(sketch, "E50.0.2.6", {"start": v(-37, 4863.17) * mm, "end": v(-1, 4931.17) * mm});
            skLineSegment(sketch, "E50.0.2.7", {"start": v(-1, 4447.17) * mm, "end": v(-37, 4515.17) * mm});
            skLineSegment(sketch, "E50.0.2.8", {"start": v(-36, 4863.17) * mm, "end": v(0, 4931.17) * mm});
            skLineSegment(sketch, "E50.0.2.9", {"start": v(-36, 4515.17) * mm, "end": v(-36, 4585.17) * mm});
            skLineSegment(sketch, "E50.0.2.10", {"start": v(-37, 4237.17) * mm, "end": v(-37, 4307.17) * mm});
            skLineSegment(sketch, "E50.0.2.11", {"start": v(-36, 4793.17) * mm, "end": v(-36, 4863.17) * mm});
            skLineSegment(sketch, "E50.0.2.12", {"start": v(-1, 4653.17) * mm, "end": v(-1, 4725.17) * mm});
            skLineSegment(sketch, "E50.0.2.13", {"start": v(-37, 4307.17) * mm, "end": v(-1, 4375.17) * mm});
            skLineSegment(sketch, "E50.0.2.14", {"start": v(-36, 4307.17) * mm, "end": v(0, 4375.17) * mm});
            skLineSegment(sketch, "E50.0.2.15", {"start": v(0, 4931.17) * mm, "end": v(0, 5003.17) * mm});
            skLineSegment(sketch, "E50.0.2.16", {"start": v(0, 4447.17) * mm, "end": v(-36, 4515.17) * mm});
            skLineSegment(sketch, "E50.0.2.17", {"start": v(-36, 4237.17) * mm, "end": v(-36, 4307.17) * mm});
            skLineSegment(sketch, "E50.0.2.18", {"start": v(-1, 4375.17) * mm, "end": v(-1, 4447.17) * mm});
            skLineSegment(sketch, "E50.0.2.19", {"start": v(-36, 4585.17) * mm, "end": v(0, 4653.17) * mm});
            skLineSegment(sketch, "E50.0.2.20", {"start": v(-1, 4931.17) * mm, "end": v(-1, 5003.17) * mm});
            skLineSegment(sketch, "E50.0.2.21", {"start": v(-37, 4793.17) * mm, "end": v(-37, 4863.17) * mm});
            skLineSegment(sketch, "E50.0.2.22", {"start": v(-36, 5697.17) * mm, "end": v(-36, 5975.17) * mm, "construction": true});
            skLineSegment(sketch, "E50.0.2.23", {"start": v(0, 6115.17) * mm, "end": v(-36, 6183.17) * mm});
            skLineSegment(sketch, "E50.0.2.24", {"start": v(-1, 6115.17) * mm, "end": v(-37, 6183.17) * mm});
            skLineSegment(sketch, "E50.0.2.25", {"start": v(-37, 5697.17) * mm, "end": v(-37, 5975.17) * mm, "construction": true});
            skLineSegment(sketch, "E50.0.2.26", {"start": v(-1, 5281.17) * mm, "end": v(-37, 5349.17) * mm});
            skLineSegment(sketch, "E50.0.2.27", {"start": v(0, 5281.17) * mm, "end": v(-36, 5349.17) * mm});
            skLineSegment(sketch, "E50.0.2.28", {"start": v(0, 6043.17) * mm, "end": v(0, 6115.17) * mm});
            skLineSegment(sketch, "E50.0.2.29", {"start": v(-36, 5975.17) * mm, "end": v(0, 6043.17) * mm});
            skLineSegment(sketch, "E50.0.2.30", {"start": v(0, 5209.17) * mm, "end": v(0, 5281.17) * mm});
            skLineSegment(sketch, "E50.0.2.31", {"start": v(-1, 5209.17) * mm, "end": v(-1, 5281.17) * mm});
            skLineSegment(sketch, "E50.0.2.32", {"start": v(-37, 5975.17) * mm, "end": v(-1, 6043.17) * mm});
            skLineSegment(sketch, "E50.0.2.33", {"start": v(-1, 6043.17) * mm, "end": v(-1, 6115.17) * mm});
            skLineSegment(sketch, "E50.0.2.34", {"start": v(-37, 5627.17) * mm, "end": v(-37, 5697.17) * mm});
            skLineSegment(sketch, "E50.0.2.35", {"start": v(-1, 5487.17) * mm, "end": v(-1, 5559.17) * mm});
            skLineSegment(sketch, "E50.0.2.36", {"start": v(-37, 5071.17) * mm, "end": v(-37, 5141.17) * mm});
            skLineSegment(sketch, "E50.0.2.37", {"start": v(-1, 5837.17) * mm, "end": v(-37, 5905.17) * mm});
            skLineSegment(sketch, "E50.0.2.38", {"start": v(-36, 5419.17) * mm, "end": v(0, 5487.17) * mm});
            skLineSegment(sketch, "E50.0.2.39", {"start": v(-1, 5559.17) * mm, "end": v(-37, 5627.17) * mm});
            skLineSegment(sketch, "E50.0.2.40", {"start": v(0, 5765.17) * mm, "end": v(0, 5837.17) * mm});
            skLineSegment(sketch, "E50.0.2.41", {"start": v(-36, 5697.17) * mm, "end": v(0, 5765.17) * mm});
            skLineSegment(sketch, "E50.0.2.42", {"start": v(0, 5487.17) * mm, "end": v(0, 5559.17) * mm});
            skLineSegment(sketch, "E50.0.2.43", {"start": v(-36, 5071.17) * mm, "end": v(-36, 5141.17) * mm});
            skLineSegment(sketch, "E50.0.2.44", {"start": v(-37, 5419.17) * mm, "end": v(-1, 5487.17) * mm});
            skLineSegment(sketch, "E50.0.2.45", {"start": v(-37, 5141.17) * mm, "end": v(-1, 5209.17) * mm});
            skLineSegment(sketch, "E50.0.2.46", {"start": v(-1, 5003.17) * mm, "end": v(-37, 5071.17) * mm});
            skLineSegment(sketch, "E50.0.2.47", {"start": v(-1, 5765.17) * mm, "end": v(-1, 5837.17) * mm});
            skLineSegment(sketch, "E50.0.2.48", {"start": v(-37, 5349.17) * mm, "end": v(-37, 5419.17) * mm});
            skLineSegment(sketch, "E50.0.2.49", {"start": v(-37, 5905.17) * mm, "end": v(-37, 5975.17) * mm});
            skLineSegment(sketch, "E50.0.2.50", {"start": v(-36, 5349.17) * mm, "end": v(-36, 5419.17) * mm});
            skLineSegment(sketch, "E50.0.2.51", {"start": v(0, 5003.17) * mm, "end": v(-36, 5071.17) * mm});
            skLineSegment(sketch, "E50.0.2.52", {"start": v(-36, 5141.17) * mm, "end": v(0, 5209.17) * mm});
            skLineSegment(sketch, "E50.0.2.53", {"start": v(-36, 5905.17) * mm, "end": v(-36, 5975.17) * mm});
            skLineSegment(sketch, "E50.0.2.54", {"start": v(-36, 5627.17) * mm, "end": v(-36, 5697.17) * mm});
            skLineSegment(sketch, "E50.0.2.55", {"start": v(0, 5837.17) * mm, "end": v(-36, 5905.17) * mm});
            skLineSegment(sketch, "E50.0.2.56", {"start": v(0, 5559.17) * mm, "end": v(-36, 5627.17) * mm});
            skLineSegment(sketch, "E50.0.2.57", {"start": v(-37, 5697.17) * mm, "end": v(-1, 5765.17) * mm});
            skLineSegment(sketch, "E50.0.3.0", {"start": v(0, 6671.17) * mm, "end": v(-36, 6739.17) * mm});
            skLineSegment(sketch, "E50.0.3.1", {"start": v(-1, 6671.17) * mm, "end": v(-37, 6739.17) * mm});
            skLineSegment(sketch, "E50.0.3.2", {"start": v(0, 6599.17) * mm, "end": v(0, 6671.17) * mm});
            skLineSegment(sketch, "E50.0.3.3", {"start": v(0, 6321.17) * mm, "end": v(0, 6393.17) * mm});
            skLineSegment(sketch, "E50.0.3.4", {"start": v(-37, 6531.17) * mm, "end": v(-1, 6599.17) * mm});
            skLineSegment(sketch, "E50.0.3.5", {"start": v(-37, 6461.17) * mm, "end": v(-37, 6531.17) * mm});
            skLineSegment(sketch, "E50.0.3.6", {"start": v(-37, 6809.17) * mm, "end": v(-1, 6877.17) * mm});
            skLineSegment(sketch, "E50.0.3.7", {"start": v(-1, 6393.17) * mm, "end": v(-37, 6461.17) * mm});
            skLineSegment(sketch, "E50.0.3.8", {"start": v(-36, 6809.17) * mm, "end": v(0, 6877.17) * mm});
            skLineSegment(sketch, "E50.0.3.9", {"start": v(-36, 6461.17) * mm, "end": v(-36, 6531.17) * mm});
            skLineSegment(sketch, "E50.0.3.10", {"start": v(-37, 6183.17) * mm, "end": v(-37, 6253.17) * mm});
            skLineSegment(sketch, "E50.0.3.11", {"start": v(-36, 6739.17) * mm, "end": v(-36, 6809.17) * mm});
            skLineSegment(sketch, "E50.0.3.12", {"start": v(-1, 6599.17) * mm, "end": v(-1, 6671.17) * mm});
            skLineSegment(sketch, "E50.0.3.13", {"start": v(-37, 6253.17) * mm, "end": v(-1, 6321.17) * mm});
            skLineSegment(sketch, "E50.0.3.14", {"start": v(-36, 6253.17) * mm, "end": v(0, 6321.17) * mm});
            skLineSegment(sketch, "E50.0.3.15", {"start": v(0, 6877.17) * mm, "end": v(0, 6949.17) * mm});
            skLineSegment(sketch, "E50.0.3.16", {"start": v(0, 6393.17) * mm, "end": v(-36, 6461.17) * mm});
            skLineSegment(sketch, "E50.0.3.17", {"start": v(-36, 6183.17) * mm, "end": v(-36, 6253.17) * mm});
            skLineSegment(sketch, "E50.0.3.18", {"start": v(-1, 6321.17) * mm, "end": v(-1, 6393.17) * mm});
            skLineSegment(sketch, "E50.0.3.19", {"start": v(-36, 6531.17) * mm, "end": v(0, 6599.17) * mm});
            skLineSegment(sketch, "E50.0.3.20", {"start": v(-1, 6877.17) * mm, "end": v(-1, 6949.17) * mm});
            skLineSegment(sketch, "E50.0.3.21", {"start": v(-37, 6739.17) * mm, "end": v(-37, 6809.17) * mm});
            skLineSegment(sketch, "E50.0.3.22", {"start": v(-36, 7643.17) * mm, "end": v(-36, 7921.17) * mm, "construction": true});
            skLineSegment(sketch, "E50.0.3.23", {"start": v(0, 8061.17) * mm, "end": v(-36, 8129.17) * mm});
            skLineSegment(sketch, "E50.0.3.24", {"start": v(-1, 8061.17) * mm, "end": v(-37, 8129.17) * mm});
            skLineSegment(sketch, "E50.0.3.25", {"start": v(-37, 7643.17) * mm, "end": v(-37, 7921.17) * mm, "construction": true});
            skLineSegment(sketch, "E50.0.3.26", {"start": v(-1, 7227.17) * mm, "end": v(-37, 7295.17) * mm});
            skLineSegment(sketch, "E50.0.3.27", {"start": v(0, 7227.17) * mm, "end": v(-36, 7295.17) * mm});
            skLineSegment(sketch, "E50.0.3.28", {"start": v(0, 7989.17) * mm, "end": v(0, 8061.17) * mm});
            skLineSegment(sketch, "E50.0.3.29", {"start": v(-36, 7921.17) * mm, "end": v(0, 7989.17) * mm});
            skLineSegment(sketch, "E50.0.3.30", {"start": v(0, 7155.17) * mm, "end": v(0, 7227.17) * mm});
            skLineSegment(sketch, "E50.0.3.31", {"start": v(-1, 7155.17) * mm, "end": v(-1, 7227.17) * mm});
            skLineSegment(sketch, "E50.0.3.32", {"start": v(-37, 7921.17) * mm, "end": v(-1, 7989.17) * mm});
            skLineSegment(sketch, "E50.0.3.33", {"start": v(-1, 7989.17) * mm, "end": v(-1, 8061.17) * mm});
            skLineSegment(sketch, "E50.0.3.34", {"start": v(-37, 7573.17) * mm, "end": v(-37, 7643.17) * mm});
            skLineSegment(sketch, "E50.0.3.35", {"start": v(-1, 7433.17) * mm, "end": v(-1, 7505.17) * mm});
            skLineSegment(sketch, "E50.0.3.36", {"start": v(-37, 7017.17) * mm, "end": v(-37, 7087.17) * mm});
            skLineSegment(sketch, "E50.0.3.37", {"start": v(-1, 7783.17) * mm, "end": v(-37, 7851.17) * mm});
            skLineSegment(sketch, "E50.0.3.38", {"start": v(-36, 7365.17) * mm, "end": v(0, 7433.17) * mm});
            skLineSegment(sketch, "E50.0.3.39", {"start": v(-1, 7505.17) * mm, "end": v(-37, 7573.17) * mm});
            skLineSegment(sketch, "E50.0.3.40", {"start": v(0, 7711.17) * mm, "end": v(0, 7783.17) * mm});
            skLineSegment(sketch, "E50.0.3.41", {"start": v(-36, 7643.17) * mm, "end": v(0, 7711.17) * mm});
            skLineSegment(sketch, "E50.0.3.42", {"start": v(0, 7433.17) * mm, "end": v(0, 7505.17) * mm});
            skLineSegment(sketch, "E50.0.3.43", {"start": v(-36, 7017.17) * mm, "end": v(-36, 7087.17) * mm});
            skLineSegment(sketch, "E50.0.3.44", {"start": v(-37, 7365.17) * mm, "end": v(-1, 7433.17) * mm});
            skLineSegment(sketch, "E50.0.3.45", {"start": v(-37, 7087.17) * mm, "end": v(-1, 7155.17) * mm});
            skLineSegment(sketch, "E50.0.3.46", {"start": v(-1, 6949.17) * mm, "end": v(-37, 7017.17) * mm});
            skLineSegment(sketch, "E50.0.3.47", {"start": v(-1, 7711.17) * mm, "end": v(-1, 7783.17) * mm});
            skLineSegment(sketch, "E50.0.3.48", {"start": v(-37, 7295.17) * mm, "end": v(-37, 7365.17) * mm});
            skLineSegment(sketch, "E50.0.3.49", {"start": v(-37, 7851.17) * mm, "end": v(-37, 7921.17) * mm});
            skLineSegment(sketch, "E50.0.3.50", {"start": v(-36, 7295.17) * mm, "end": v(-36, 7365.17) * mm});
            skLineSegment(sketch, "E50.0.3.51", {"start": v(0, 6949.17) * mm, "end": v(-36, 7017.17) * mm});
            skLineSegment(sketch, "E50.0.3.52", {"start": v(-36, 7087.17) * mm, "end": v(0, 7155.17) * mm});
            skLineSegment(sketch, "E50.0.3.53", {"start": v(-36, 7851.17) * mm, "end": v(-36, 7921.17) * mm});
            skLineSegment(sketch, "E50.0.3.54", {"start": v(-36, 7573.17) * mm, "end": v(-36, 7643.17) * mm});
            skLineSegment(sketch, "E50.0.3.55", {"start": v(0, 7783.17) * mm, "end": v(-36, 7851.17) * mm});
            skLineSegment(sketch, "E50.0.3.56", {"start": v(0, 7505.17) * mm, "end": v(-36, 7573.17) * mm});
            skLineSegment(sketch, "E50.0.3.57", {"start": v(-37, 7643.17) * mm, "end": v(-1, 7711.17) * mm});
            skLineSegment(sketch, "E50.0.4.0", {"start": v(0, 8617.17) * mm, "end": v(-36, 8685.17) * mm});
            skLineSegment(sketch, "E50.0.4.1", {"start": v(-1, 8617.17) * mm, "end": v(-37, 8685.17) * mm});
            skLineSegment(sketch, "E50.0.4.2", {"start": v(0, 8545.17) * mm, "end": v(0, 8617.17) * mm});
            skLineSegment(sketch, "E50.0.4.3", {"start": v(0, 8267.17) * mm, "end": v(0, 8339.17) * mm});
            skLineSegment(sketch, "E50.0.4.4", {"start": v(-37, 8477.17) * mm, "end": v(-1, 8545.17) * mm});
            skLineSegment(sketch, "E50.0.4.5", {"start": v(-37, 8407.17) * mm, "end": v(-37, 8477.17) * mm});
            skLineSegment(sketch, "E50.0.4.6", {"start": v(-37, 8755.17) * mm, "end": v(-1, 8823.17) * mm});
            skLineSegment(sketch, "E50.0.4.7", {"start": v(-1, 8339.17) * mm, "end": v(-37, 8407.17) * mm});
            skLineSegment(sketch, "E50.0.4.8", {"start": v(-36, 8755.17) * mm, "end": v(0, 8823.17) * mm});
            skLineSegment(sketch, "E50.0.4.9", {"start": v(-36, 8407.17) * mm, "end": v(-36, 8477.17) * mm});
            skLineSegment(sketch, "E50.0.4.10", {"start": v(-37, 8129.17) * mm, "end": v(-37, 8199.17) * mm});
            skLineSegment(sketch, "E50.0.4.11", {"start": v(-36, 8685.17) * mm, "end": v(-36, 8755.17) * mm});
            skLineSegment(sketch, "E50.0.4.12", {"start": v(-1, 8545.17) * mm, "end": v(-1, 8617.17) * mm});
            skLineSegment(sketch, "E50.0.4.13", {"start": v(-37, 8199.17) * mm, "end": v(-1, 8267.17) * mm});
            skLineSegment(sketch, "E50.0.4.14", {"start": v(-36, 8199.17) * mm, "end": v(0, 8267.17) * mm});
            skLineSegment(sketch, "E50.0.4.15", {"start": v(0, 8823.17) * mm, "end": v(0, 8895.17) * mm});
            skLineSegment(sketch, "E50.0.4.16", {"start": v(0, 8339.17) * mm, "end": v(-36, 8407.17) * mm});
            skLineSegment(sketch, "E50.0.4.17", {"start": v(-36, 8129.17) * mm, "end": v(-36, 8199.17) * mm});
            skLineSegment(sketch, "E50.0.4.18", {"start": v(-1, 8267.17) * mm, "end": v(-1, 8339.17) * mm});
            skLineSegment(sketch, "E50.0.4.19", {"start": v(-36, 8477.17) * mm, "end": v(0, 8545.17) * mm});
            skLineSegment(sketch, "E50.0.4.20", {"start": v(-1, 8823.17) * mm, "end": v(-1, 8895.17) * mm});
            skLineSegment(sketch, "E50.0.4.21", {"start": v(-37, 8685.17) * mm, "end": v(-37, 8755.17) * mm});
            skLineSegment(sketch, "E50.0.4.22", {"start": v(-36, 9589.17) * mm, "end": v(-36, 9867.17) * mm, "construction": true});
            skLineSegment(sketch, "E50.0.4.23", {"start": v(0, 10007.17) * mm, "end": v(-36, 10075.17) * mm});
            skLineSegment(sketch, "E50.0.4.24", {"start": v(-1, 10007.17) * mm, "end": v(-37, 10075.17) * mm});
            skLineSegment(sketch, "E50.0.4.25", {"start": v(-37, 9589.17) * mm, "end": v(-37, 9867.17) * mm, "construction": true});
            skLineSegment(sketch, "E50.0.4.26", {"start": v(-1, 9173.17) * mm, "end": v(-37, 9241.17) * mm});
            skLineSegment(sketch, "E50.0.4.27", {"start": v(0, 9173.17) * mm, "end": v(-36, 9241.17) * mm});
            skLineSegment(sketch, "E50.0.4.28", {"start": v(0, 9935.17) * mm, "end": v(0, 10007.17) * mm});
            skLineSegment(sketch, "E50.0.4.29", {"start": v(-36, 9867.17) * mm, "end": v(0, 9935.17) * mm});
            skLineSegment(sketch, "E50.0.4.30", {"start": v(0, 9101.17) * mm, "end": v(0, 9173.17) * mm});
            skLineSegment(sketch, "E50.0.4.31", {"start": v(-1, 9101.17) * mm, "end": v(-1, 9173.17) * mm});
            skLineSegment(sketch, "E50.0.4.32", {"start": v(-37, 9867.17) * mm, "end": v(-1, 9935.17) * mm});
            skLineSegment(sketch, "E50.0.4.33", {"start": v(-1, 9935.17) * mm, "end": v(-1, 10007.17) * mm});
            skLineSegment(sketch, "E50.0.4.34", {"start": v(-37, 9519.17) * mm, "end": v(-37, 9589.17) * mm});
            skLineSegment(sketch, "E50.0.4.35", {"start": v(-1, 9379.17) * mm, "end": v(-1, 9451.17) * mm});
            skLineSegment(sketch, "E50.0.4.36", {"start": v(-37, 8963.17) * mm, "end": v(-37, 9033.17) * mm});
            skLineSegment(sketch, "E50.0.4.37", {"start": v(-1, 9729.17) * mm, "end": v(-37, 9797.17) * mm});
            skLineSegment(sketch, "E50.0.4.38", {"start": v(-36, 9311.17) * mm, "end": v(0, 9379.17) * mm});
            skLineSegment(sketch, "E50.0.4.39", {"start": v(-1, 9451.17) * mm, "end": v(-37, 9519.17) * mm});
            skLineSegment(sketch, "E50.0.4.40", {"start": v(0, 9657.17) * mm, "end": v(0, 9729.17) * mm});
            skLineSegment(sketch, "E50.0.4.41", {"start": v(-36, 9589.17) * mm, "end": v(0, 9657.17) * mm});
            skLineSegment(sketch, "E50.0.4.42", {"start": v(0, 9379.17) * mm, "end": v(0, 9451.17) * mm});
            skLineSegment(sketch, "E50.0.4.43", {"start": v(-36, 8963.17) * mm, "end": v(-36, 9033.17) * mm});
            skLineSegment(sketch, "E50.0.4.44", {"start": v(-37, 9311.17) * mm, "end": v(-1, 9379.17) * mm});
            skLineSegment(sketch, "E50.0.4.45", {"start": v(-37, 9033.17) * mm, "end": v(-1, 9101.17) * mm});
            skLineSegment(sketch, "E50.0.4.46", {"start": v(-1, 8895.17) * mm, "end": v(-37, 8963.17) * mm});
            skLineSegment(sketch, "E50.0.4.47", {"start": v(-1, 9657.17) * mm, "end": v(-1, 9729.17) * mm});
            skLineSegment(sketch, "E50.0.4.48", {"start": v(-37, 9241.17) * mm, "end": v(-37, 9311.17) * mm});
            skLineSegment(sketch, "E50.0.4.49", {"start": v(-37, 9797.17) * mm, "end": v(-37, 9867.17) * mm});
            skLineSegment(sketch, "E50.0.4.50", {"start": v(-36, 9241.17) * mm, "end": v(-36, 9311.17) * mm});
            skLineSegment(sketch, "E50.0.4.51", {"start": v(0, 8895.17) * mm, "end": v(-36, 8963.17) * mm});
            skLineSegment(sketch, "E50.0.4.52", {"start": v(-36, 9033.17) * mm, "end": v(0, 9101.17) * mm});
            skLineSegment(sketch, "E50.0.4.53", {"start": v(-36, 9797.17) * mm, "end": v(-36, 9867.17) * mm});
            skLineSegment(sketch, "E50.0.4.54", {"start": v(-36, 9519.17) * mm, "end": v(-36, 9589.17) * mm});
            skLineSegment(sketch, "E50.0.4.55", {"start": v(0, 9729.17) * mm, "end": v(-36, 9797.17) * mm});
            skLineSegment(sketch, "E50.0.4.56", {"start": v(0, 9451.17) * mm, "end": v(-36, 9519.17) * mm});
            skLineSegment(sketch, "E50.0.4.57", {"start": v(-37, 9589.17) * mm, "end": v(-1, 9657.17) * mm});
            skLineSegment(sketch, "E50.0.5.0", {"start": v(0, 10563.17) * mm, "end": v(-36, 10631.17) * mm});
            skLineSegment(sketch, "E50.0.5.1", {"start": v(-1, 10563.17) * mm, "end": v(-37, 10631.17) * mm});
            skLineSegment(sketch, "E50.0.5.2", {"start": v(0, 10491.17) * mm, "end": v(0, 10563.17) * mm});
            skLineSegment(sketch, "E50.0.5.3", {"start": v(0, 10213.17) * mm, "end": v(0, 10285.17) * mm});
            skLineSegment(sketch, "E50.0.5.4", {"start": v(-37, 10423.17) * mm, "end": v(-1, 10491.17) * mm});
            skLineSegment(sketch, "E50.0.5.5", {"start": v(-37, 10353.17) * mm, "end": v(-37, 10423.17) * mm});
            skLineSegment(sketch, "E50.0.5.6", {"start": v(-37, 10701.17) * mm, "end": v(-1, 10769.17) * mm});
            skLineSegment(sketch, "E50.0.5.7", {"start": v(-1, 10285.17) * mm, "end": v(-37, 10353.17) * mm});
            skLineSegment(sketch, "E50.0.5.8", {"start": v(-36, 10701.17) * mm, "end": v(0, 10769.17) * mm});
            skLineSegment(sketch, "E50.0.5.9", {"start": v(-36, 10353.17) * mm, "end": v(-36, 10423.17) * mm});
            skLineSegment(sketch, "E50.0.5.10", {"start": v(-37, 10075.17) * mm, "end": v(-37, 10145.17) * mm});
            skLineSegment(sketch, "E50.0.5.11", {"start": v(-36, 10631.17) * mm, "end": v(-36, 10701.17) * mm});
            skLineSegment(sketch, "E50.0.5.12", {"start": v(-1, 10491.17) * mm, "end": v(-1, 10563.17) * mm});
            skLineSegment(sketch, "E50.0.5.13", {"start": v(-37, 10145.17) * mm, "end": v(-1, 10213.17) * mm});
            skLineSegment(sketch, "E50.0.5.14", {"start": v(-36, 10145.17) * mm, "end": v(0, 10213.17) * mm});
            skLineSegment(sketch, "E50.0.5.15", {"start": v(0, 10769.17) * mm, "end": v(0, 10841.17) * mm});
            skLineSegment(sketch, "E50.0.5.16", {"start": v(0, 10285.17) * mm, "end": v(-36, 10353.17) * mm});
            skLineSegment(sketch, "E50.0.5.17", {"start": v(-36, 10075.17) * mm, "end": v(-36, 10145.17) * mm});
            skLineSegment(sketch, "E50.0.5.18", {"start": v(-1, 10213.17) * mm, "end": v(-1, 10285.17) * mm});
            skLineSegment(sketch, "E50.0.5.19", {"start": v(-36, 10423.17) * mm, "end": v(0, 10491.17) * mm});
            skLineSegment(sketch, "E50.0.5.20", {"start": v(-1, 10769.17) * mm, "end": v(-1, 10841.17) * mm});
            skLineSegment(sketch, "E50.0.5.21", {"start": v(-37, 10631.17) * mm, "end": v(-37, 10701.17) * mm});
            skLineSegment(sketch, "E50.0.5.22", {"start": v(-36, 11535.17) * mm, "end": v(-36, 11813.17) * mm, "construction": true});
            skLineSegment(sketch, "E50.0.5.23", {"start": v(0, 11953.17) * mm, "end": v(-36, 12021.17) * mm});
            skLineSegment(sketch, "E50.0.5.24", {"start": v(-1, 11953.17) * mm, "end": v(-37, 12021.17) * mm});
            skLineSegment(sketch, "E50.0.5.25", {"start": v(-37, 11535.17) * mm, "end": v(-37, 11813.17) * mm, "construction": true});
            skLineSegment(sketch, "E50.0.5.26", {"start": v(-1, 11119.17) * mm, "end": v(-37, 11187.17) * mm});
            skLineSegment(sketch, "E50.0.5.27", {"start": v(0, 11119.17) * mm, "end": v(-36, 11187.17) * mm});
            skLineSegment(sketch, "E50.0.5.28", {"start": v(0, 11881.17) * mm, "end": v(0, 11953.17) * mm});
            skLineSegment(sketch, "E50.0.5.29", {"start": v(-36, 11813.17) * mm, "end": v(0, 11881.17) * mm});
            skLineSegment(sketch, "E50.0.5.30", {"start": v(0, 11047.17) * mm, "end": v(0, 11119.17) * mm});
            skLineSegment(sketch, "E50.0.5.31", {"start": v(-1, 11047.17) * mm, "end": v(-1, 11119.17) * mm});
            skLineSegment(sketch, "E50.0.5.32", {"start": v(-37, 11813.17) * mm, "end": v(-1, 11881.17) * mm});
            skLineSegment(sketch, "E50.0.5.33", {"start": v(-1, 11881.17) * mm, "end": v(-1, 11953.17) * mm});
            skLineSegment(sketch, "E50.0.5.34", {"start": v(-37, 11465.17) * mm, "end": v(-37, 11535.17) * mm});
            skLineSegment(sketch, "E50.0.5.35", {"start": v(-1, 11325.17) * mm, "end": v(-1, 11397.17) * mm});
            skLineSegment(sketch, "E50.0.5.36", {"start": v(-37, 10909.17) * mm, "end": v(-37, 10979.17) * mm});
            skLineSegment(sketch, "E50.0.5.37", {"start": v(-1, 11675.17) * mm, "end": v(-37, 11743.17) * mm});
            skLineSegment(sketch, "E50.0.5.38", {"start": v(-36, 11257.17) * mm, "end": v(0, 11325.17) * mm});
            skLineSegment(sketch, "E50.0.5.39", {"start": v(-1, 11397.17) * mm, "end": v(-37, 11465.17) * mm});
            skLineSegment(sketch, "E50.0.5.40", {"start": v(0, 11603.17) * mm, "end": v(0, 11675.17) * mm});
            skLineSegment(sketch, "E50.0.5.41", {"start": v(-36, 11535.17) * mm, "end": v(0, 11603.17) * mm});
            skLineSegment(sketch, "E50.0.5.42", {"start": v(0, 11325.17) * mm, "end": v(0, 11397.17) * mm});
            skLineSegment(sketch, "E50.0.5.43", {"start": v(-36, 10909.17) * mm, "end": v(-36, 10979.17) * mm});
            skLineSegment(sketch, "E50.0.5.44", {"start": v(-37, 11257.17) * mm, "end": v(-1, 11325.17) * mm});
            skLineSegment(sketch, "E50.0.5.45", {"start": v(-37, 10979.17) * mm, "end": v(-1, 11047.17) * mm});
            skLineSegment(sketch, "E50.0.5.46", {"start": v(-1, 10841.17) * mm, "end": v(-37, 10909.17) * mm});
            skLineSegment(sketch, "E50.0.5.47", {"start": v(-1, 11603.17) * mm, "end": v(-1, 11675.17) * mm});
            skLineSegment(sketch, "E50.0.5.48", {"start": v(-37, 11187.17) * mm, "end": v(-37, 11257.17) * mm});
            skLineSegment(sketch, "E50.0.5.49", {"start": v(-37, 11743.17) * mm, "end": v(-37, 11813.17) * mm});
            skLineSegment(sketch, "E50.0.5.50", {"start": v(-36, 11187.17) * mm, "end": v(-36, 11257.17) * mm});
            skLineSegment(sketch, "E50.0.5.51", {"start": v(0, 10841.17) * mm, "end": v(-36, 10909.17) * mm});
            skLineSegment(sketch, "E50.0.5.52", {"start": v(-36, 10979.17) * mm, "end": v(0, 11047.17) * mm});
            skLineSegment(sketch, "E50.0.5.53", {"start": v(-36, 11743.17) * mm, "end": v(-36, 11813.17) * mm});
            skLineSegment(sketch, "E50.0.5.54", {"start": v(-36, 11465.17) * mm, "end": v(-36, 11535.17) * mm});
            skLineSegment(sketch, "E50.0.5.55", {"start": v(0, 11675.17) * mm, "end": v(-36, 11743.17) * mm});
            skLineSegment(sketch, "E50.0.5.56", {"start": v(0, 11397.17) * mm, "end": v(-36, 11465.17) * mm});
            skLineSegment(sketch, "E50.0.5.57", {"start": v(-37, 11535.17) * mm, "end": v(-1, 11603.17) * mm});
            skLineSegment(sketch, "E50.direction1", {"start": v(-37, 345.17) * mm, "end": v(-12, 345.17) * mm, "construction": true});
            skLineSegment(sketch, "E50.direction2", {"start": v(-37, 345.17) * mm, "end": v(-37, 2291.17) * mm, "construction": true});
            skLineSegment(sketch, "E51", {"start": v(-36, 12021.17) * mm, "end": v(-36, 12092) * mm});
            skLineSegment(sketch, "E52", {"start": v(-36, 12092) * mm, "end": v(-37, 12092) * mm});
            skLineSegment(sketch, "E53", {"start": v(-37, 12092) * mm, "end": v(-37, 12021.17) * mm});
            skSolve(sketch);
        }
        {
            var Q0;
            Q0=qSketchRegion(id+"F12",true);
            extrude(context, id + "F13", {"entities" : qUnion([Q0]), "operationType" : NewBodyOperationType.ADD, "depth" : 2696 * mm, "offsetDistance" : 25 * mm});
        }
        {
            var Q0;
            Q0=makeQuery(id+"F7.boolean.opBoolean","COPY",FACE,{"derivedFrom":makeQuery(id+"F7.opExtrude","SWEPT_FACE",FACE,{"disambiguationData":[OSD([sQuery(id+"F6.wireOp",EDGE,"E12")])]})});
            var sketch = newSketch(context, id + "F14", { "sketchPlane" : qUnion([Q0])});
            skLineSegment(sketch, "E54", {"start": v(12091.83, 2859.97) * mm, "end": v(12054.83, 2859.97) * mm});
            skLineSegment(sketch, "E55", {"start": v(11986.83, 2895.97) * mm, "end": v(11914.83, 2895.97) * mm});
            skLineSegment(sketch, "E56", {"start": v(11846.83, 2859.97) * mm, "end": v(11776.83, 2859.97) * mm});
            skLineSegment(sketch, "E57", {"start": v(12054.83, 2859.97) * mm, "end": v(11986.83, 2895.97) * mm});
            skLineSegment(sketch, "E58", {"start": v(11914.83, 2895.97) * mm, "end": v(11846.83, 2859.97) * mm});
            skLineSegment(sketch, "E59.1.0.0", {"start": v(11776.83, 2859.97) * mm, "end": v(11708.83, 2895.97) * mm});
            skLineSegment(sketch, "E59.1.0.1", {"start": v(11708.83, 2895.97) * mm, "end": v(11636.83, 2895.97) * mm});
            skLineSegment(sketch, "E59.1.0.2", {"start": v(11636.83, 2895.97) * mm, "end": v(11568.83, 2859.97) * mm});
            skLineSegment(sketch, "E59.1.0.3", {"start": v(11568.83, 2859.97) * mm, "end": v(11498.83, 2859.97) * mm});
            skLineSegment(sketch, "E59.2.0.0", {"start": v(11498.83, 2859.97) * mm, "end": v(11430.83, 2895.97) * mm});
            skLineSegment(sketch, "E59.2.0.1", {"start": v(11430.83, 2895.97) * mm, "end": v(11358.83, 2895.97) * mm});
            skLineSegment(sketch, "E59.2.0.2", {"start": v(11358.83, 2895.97) * mm, "end": v(11290.83, 2859.97) * mm});
            skLineSegment(sketch, "E59.2.0.3", {"start": v(11290.83, 2859.97) * mm, "end": v(11220.83, 2859.97) * mm});
            skLineSegment(sketch, "E59.3.0.0", {"start": v(11220.83, 2859.97) * mm, "end": v(11152.83, 2895.97) * mm});
            skLineSegment(sketch, "E59.3.0.1", {"start": v(11152.83, 2895.97) * mm, "end": v(11080.83, 2895.97) * mm});
            skLineSegment(sketch, "E59.3.0.2", {"start": v(11080.83, 2895.97) * mm, "end": v(11012.83, 2859.97) * mm});
            skLineSegment(sketch, "E59.3.0.3", {"start": v(11012.83, 2859.97) * mm, "end": v(10942.83, 2859.97) * mm});
            skLineSegment(sketch, "E59.4.0.0", {"start": v(10942.83, 2859.97) * mm, "end": v(10874.83, 2895.97) * mm});
            skLineSegment(sketch, "E59.4.0.1", {"start": v(10874.83, 2895.97) * mm, "end": v(10802.83, 2895.97) * mm});
            skLineSegment(sketch, "E59.4.0.2", {"start": v(10802.83, 2895.97) * mm, "end": v(10734.83, 2859.97) * mm});
            skLineSegment(sketch, "E59.4.0.3", {"start": v(10734.83, 2859.97) * mm, "end": v(10664.83, 2859.97) * mm});
            skLineSegment(sketch, "E59.5.0.0", {"start": v(10664.83, 2859.97) * mm, "end": v(10596.83, 2895.97) * mm});
            skLineSegment(sketch, "E59.5.0.1", {"start": v(10596.83, 2895.97) * mm, "end": v(10524.83, 2895.97) * mm});
            skLineSegment(sketch, "E59.5.0.2", {"start": v(10524.83, 2895.97) * mm, "end": v(10456.83, 2859.97) * mm});
            skLineSegment(sketch, "E59.5.0.3", {"start": v(10456.83, 2859.97) * mm, "end": v(10386.83, 2859.97) * mm});
            skLineSegment(sketch, "E59.6.0.0", {"start": v(10386.83, 2859.97) * mm, "end": v(10318.83, 2895.97) * mm});
            skLineSegment(sketch, "E59.6.0.1", {"start": v(10318.83, 2895.97) * mm, "end": v(10246.83, 2895.97) * mm});
            skLineSegment(sketch, "E59.6.0.2", {"start": v(10246.83, 2895.97) * mm, "end": v(10178.83, 2859.97) * mm});
            skLineSegment(sketch, "E59.6.0.3", {"start": v(10178.83, 2859.97) * mm, "end": v(10108.83, 2859.97) * mm});
            skLineSegment(sketch, "E59.direction1", {"start": v(12054.83, 2859.97) * mm, "end": v(11776.83, 2859.97) * mm, "construction": true});
            skLineSegment(sketch, "E60.1.0.0", {"start": v(10108.83, 2859.97) * mm, "end": v(10040.83, 2895.97) * mm});
            skLineSegment(sketch, "E60.1.0.1", {"start": v(10040.83, 2895.97) * mm, "end": v(9968.83, 2895.97) * mm});
            skLineSegment(sketch, "E60.1.0.2", {"start": v(9968.83, 2895.97) * mm, "end": v(9900.83, 2859.97) * mm});
            skLineSegment(sketch, "E60.direction1", {"start": v(10386.83, 2859.97) * mm, "end": v(10108.83, 2859.97) * mm, "construction": true});
            skLineSegment(sketch, "E61.0.1.0", {"start": v(12054.83, 2858.97) * mm, "end": v(11776.83, 2858.97) * mm, "construction": true});
            skLineSegment(sketch, "E61.0.1.1", {"start": v(10386.83, 2858.97) * mm, "end": v(10108.83, 2858.97) * mm, "construction": true});
            skLineSegment(sketch, "E61.0.1.2", {"start": v(10108.83, 2858.97) * mm, "end": v(10040.83, 2894.97) * mm});
            skLineSegment(sketch, "E61.0.1.3", {"start": v(11012.83, 2858.97) * mm, "end": v(10942.83, 2858.97) * mm});
            skLineSegment(sketch, "E61.0.1.5", {"start": v(11358.83, 2894.97) * mm, "end": v(11290.83, 2858.97) * mm});
            skLineSegment(sketch, "E61.0.1.6", {"start": v(11220.83, 2858.97) * mm, "end": v(11152.83, 2894.97) * mm});
            skLineSegment(sketch, "E61.0.1.7", {"start": v(10802.83, 2894.97) * mm, "end": v(10734.83, 2858.97) * mm});
            skLineSegment(sketch, "E61.0.1.8", {"start": v(10386.83, 2858.97) * mm, "end": v(10318.83, 2894.97) * mm});
            skLineSegment(sketch, "E61.0.1.9", {"start": v(11708.83, 2894.97) * mm, "end": v(11636.83, 2894.97) * mm});
            skLineSegment(sketch, "E61.0.1.10", {"start": v(9968.83, 2894.97) * mm, "end": v(9900.83, 2858.97) * mm});
            skLineSegment(sketch, "E61.0.1.11", {"start": v(10664.83, 2858.97) * mm, "end": v(10596.83, 2894.97) * mm});
            skLineSegment(sketch, "E61.0.1.12", {"start": v(11636.83, 2894.97) * mm, "end": v(11568.83, 2858.97) * mm});
            skLineSegment(sketch, "E61.0.1.13", {"start": v(11776.83, 2858.97) * mm, "end": v(11708.83, 2894.97) * mm});
            skLineSegment(sketch, "E61.0.1.14", {"start": v(10246.83, 2894.97) * mm, "end": v(10178.83, 2858.97) * mm});
            skLineSegment(sketch, "E61.0.1.15", {"start": v(11430.83, 2894.97) * mm, "end": v(11358.83, 2894.97) * mm});
            skLineSegment(sketch, "E61.0.1.16", {"start": v(10942.83, 2858.97) * mm, "end": v(10874.83, 2894.97) * mm});
            skLineSegment(sketch, "E61.0.1.17", {"start": v(11498.83, 2858.97) * mm, "end": v(11430.83, 2894.97) * mm});
            skLineSegment(sketch, "E61.0.1.18", {"start": v(10040.83, 2894.97) * mm, "end": v(9968.83, 2894.97) * mm});
            skLineSegment(sketch, "E61.0.1.19", {"start": v(10734.83, 2858.97) * mm, "end": v(10664.83, 2858.97) * mm});
            skLineSegment(sketch, "E61.0.1.20", {"start": v(10596.83, 2894.97) * mm, "end": v(10524.83, 2894.97) * mm});
            skLineSegment(sketch, "E61.0.1.21", {"start": v(10524.83, 2894.97) * mm, "end": v(10456.83, 2858.97) * mm});
            skLineSegment(sketch, "E61.0.1.22", {"start": v(11568.83, 2858.97) * mm, "end": v(11498.83, 2858.97) * mm});
            skLineSegment(sketch, "E61.0.1.23", {"start": v(10318.83, 2894.97) * mm, "end": v(10246.83, 2894.97) * mm});
            skLineSegment(sketch, "E61.0.1.24", {"start": v(11914.83, 2894.97) * mm, "end": v(11846.83, 2858.97) * mm});
            skLineSegment(sketch, "E61.0.1.25", {"start": v(10874.83, 2894.97) * mm, "end": v(10802.83, 2894.97) * mm});
            skLineSegment(sketch, "E61.0.1.26", {"start": v(12054.83, 2858.97) * mm, "end": v(11986.83, 2894.97) * mm});
            skLineSegment(sketch, "E61.0.1.27", {"start": v(11290.83, 2858.97) * mm, "end": v(11220.83, 2858.97) * mm});
            skLineSegment(sketch, "E61.0.1.28", {"start": v(11152.83, 2894.97) * mm, "end": v(11080.83, 2894.97) * mm});
            skLineSegment(sketch, "E61.0.1.29", {"start": v(11986.83, 2894.97) * mm, "end": v(11914.83, 2894.97) * mm});
            skLineSegment(sketch, "E61.0.1.30", {"start": v(11080.83, 2894.97) * mm, "end": v(11012.83, 2858.97) * mm});
            skLineSegment(sketch, "E61.0.1.31", {"start": v(10178.83, 2858.97) * mm, "end": v(10108.83, 2858.97) * mm});
            skLineSegment(sketch, "E61.0.1.32", {"start": v(11846.83, 2858.97) * mm, "end": v(11776.83, 2858.97) * mm});
            skLineSegment(sketch, "E61.0.1.33", {"start": v(10456.83, 2858.97) * mm, "end": v(10386.83, 2858.97) * mm});
            skLineSegment(sketch, "E61.0.1.34", {"start": v(12091.83, 2858.97) * mm, "end": v(12054.83, 2858.97) * mm});
            skLineSegment(sketch, "E62", {"start": v(12091.83, 2858.97) * mm, "end": v(12092, 2858.97) * mm});
            skLineSegment(sketch, "E63", {"start": v(12092, 2858.97) * mm, "end": v(12092, 2859.97) * mm});
            skLineSegment(sketch, "E64", {"start": v(12092, 2859.97) * mm, "end": v(12091.83, 2859.97) * mm});
            skLineSegment(sketch, "E65.0.1.0", {"start": v(9412.83, 2895.97) * mm, "end": v(9344.83, 2859.97) * mm});
            skLineSegment(sketch, "E65.0.1.1", {"start": v(9412.83, 2894.97) * mm, "end": v(9344.83, 2858.97) * mm});
            skLineSegment(sketch, "E65.0.1.2", {"start": v(9484.83, 2895.97) * mm, "end": v(9412.83, 2895.97) * mm});
            skLineSegment(sketch, "E65.0.1.3", {"start": v(9762.83, 2895.97) * mm, "end": v(9690.83, 2895.97) * mm});
            skLineSegment(sketch, "E65.0.1.4", {"start": v(9552.83, 2858.97) * mm, "end": v(9484.83, 2894.97) * mm});
            skLineSegment(sketch, "E65.0.1.5", {"start": v(9622.83, 2858.97) * mm, "end": v(9552.83, 2858.97) * mm});
            skLineSegment(sketch, "E65.0.1.6", {"start": v(9274.83, 2858.97) * mm, "end": v(9206.83, 2894.97) * mm});
            skLineSegment(sketch, "E65.0.1.7", {"start": v(9690.83, 2894.97) * mm, "end": v(9622.83, 2858.97) * mm});
            skLineSegment(sketch, "E65.0.1.8", {"start": v(9274.83, 2859.97) * mm, "end": v(9206.83, 2895.97) * mm});
            skLineSegment(sketch, "E65.0.1.9", {"start": v(9622.83, 2859.97) * mm, "end": v(9552.83, 2859.97) * mm});
            skLineSegment(sketch, "E65.0.1.10", {"start": v(9900.83, 2858.97) * mm, "end": v(9830.83, 2858.97) * mm});
            skLineSegment(sketch, "E65.0.1.11", {"start": v(9344.83, 2859.97) * mm, "end": v(9274.83, 2859.97) * mm});
            skLineSegment(sketch, "E65.0.1.12", {"start": v(9484.83, 2894.97) * mm, "end": v(9412.83, 2894.97) * mm});
            skLineSegment(sketch, "E65.0.1.13", {"start": v(9830.83, 2858.97) * mm, "end": v(9762.83, 2894.97) * mm});
            skLineSegment(sketch, "E65.0.1.14", {"start": v(9830.83, 2859.97) * mm, "end": v(9762.83, 2895.97) * mm});
            skLineSegment(sketch, "E65.0.1.15", {"start": v(9206.83, 2895.97) * mm, "end": v(9134.83, 2895.97) * mm});
            skLineSegment(sketch, "E65.0.1.16", {"start": v(9690.83, 2895.97) * mm, "end": v(9622.83, 2859.97) * mm});
            skLineSegment(sketch, "E65.0.1.17", {"start": v(9900.83, 2859.97) * mm, "end": v(9830.83, 2859.97) * mm});
            skLineSegment(sketch, "E65.0.1.18", {"start": v(9762.83, 2894.97) * mm, "end": v(9690.83, 2894.97) * mm});
            skLineSegment(sketch, "E65.0.1.19", {"start": v(9552.83, 2859.97) * mm, "end": v(9484.83, 2895.97) * mm});
            skLineSegment(sketch, "E65.0.1.20", {"start": v(9206.83, 2894.97) * mm, "end": v(9134.83, 2894.97) * mm});
            skLineSegment(sketch, "E65.0.1.21", {"start": v(9344.83, 2858.97) * mm, "end": v(9274.83, 2858.97) * mm});
            skLineSegment(sketch, "E65.0.1.22", {"start": v(8440.83, 2859.97) * mm, "end": v(8162.83, 2859.97) * mm, "construction": true});
            skLineSegment(sketch, "E65.0.1.23", {"start": v(8022.83, 2895.97) * mm, "end": v(7954.83, 2859.97) * mm});
            skLineSegment(sketch, "E65.0.1.24", {"start": v(8022.83, 2894.97) * mm, "end": v(7954.83, 2858.97) * mm});
            skLineSegment(sketch, "E65.0.1.25", {"start": v(8440.83, 2858.97) * mm, "end": v(8162.83, 2858.97) * mm, "construction": true});
            skLineSegment(sketch, "E65.0.1.26", {"start": v(8856.83, 2894.97) * mm, "end": v(8788.83, 2858.97) * mm});
            skLineSegment(sketch, "E65.0.1.27", {"start": v(8856.83, 2895.97) * mm, "end": v(8788.83, 2859.97) * mm});
            skLineSegment(sketch, "E65.0.1.28", {"start": v(8094.83, 2895.97) * mm, "end": v(8022.83, 2895.97) * mm});
            skLineSegment(sketch, "E65.0.1.29", {"start": v(8162.83, 2859.97) * mm, "end": v(8094.83, 2895.97) * mm});
            skLineSegment(sketch, "E65.0.1.30", {"start": v(8928.83, 2895.97) * mm, "end": v(8856.83, 2895.97) * mm});
            skLineSegment(sketch, "E65.0.1.31", {"start": v(8928.83, 2894.97) * mm, "end": v(8856.83, 2894.97) * mm});
            skLineSegment(sketch, "E65.0.1.32", {"start": v(8162.83, 2858.97) * mm, "end": v(8094.83, 2894.97) * mm});
            skLineSegment(sketch, "E65.0.1.33", {"start": v(8094.83, 2894.97) * mm, "end": v(8022.83, 2894.97) * mm});
            skLineSegment(sketch, "E65.0.1.34", {"start": v(8510.83, 2858.97) * mm, "end": v(8440.83, 2858.97) * mm});
            skLineSegment(sketch, "E65.0.1.35", {"start": v(8650.83, 2894.97) * mm, "end": v(8578.83, 2894.97) * mm});
            skLineSegment(sketch, "E65.0.1.36", {"start": v(9066.83, 2858.97) * mm, "end": v(8996.83, 2858.97) * mm});
            skLineSegment(sketch, "E65.0.1.37", {"start": v(8300.83, 2894.97) * mm, "end": v(8232.83, 2858.97) * mm});
            skLineSegment(sketch, "E65.0.1.38", {"start": v(8718.83, 2859.97) * mm, "end": v(8650.83, 2895.97) * mm});
            skLineSegment(sketch, "E65.0.1.39", {"start": v(8578.83, 2894.97) * mm, "end": v(8510.83, 2858.97) * mm});
            skLineSegment(sketch, "E65.0.1.40", {"start": v(8372.83, 2895.97) * mm, "end": v(8300.83, 2895.97) * mm});
            skLineSegment(sketch, "E65.0.1.41", {"start": v(8440.83, 2859.97) * mm, "end": v(8372.83, 2895.97) * mm});
            skLineSegment(sketch, "E65.0.1.42", {"start": v(8650.83, 2895.97) * mm, "end": v(8578.83, 2895.97) * mm});
            skLineSegment(sketch, "E65.0.1.43", {"start": v(9066.83, 2859.97) * mm, "end": v(8996.83, 2859.97) * mm});
            skLineSegment(sketch, "E65.0.1.44", {"start": v(8718.83, 2858.97) * mm, "end": v(8650.83, 2894.97) * mm});
            skLineSegment(sketch, "E65.0.1.45", {"start": v(8996.83, 2858.97) * mm, "end": v(8928.83, 2894.97) * mm});
            skLineSegment(sketch, "E65.0.1.46", {"start": v(9134.83, 2894.97) * mm, "end": v(9066.83, 2858.97) * mm});
            skLineSegment(sketch, "E65.0.1.47", {"start": v(8372.83, 2894.97) * mm, "end": v(8300.83, 2894.97) * mm});
            skLineSegment(sketch, "E65.0.1.48", {"start": v(8788.83, 2858.97) * mm, "end": v(8718.83, 2858.97) * mm});
            skLineSegment(sketch, "E65.0.1.49", {"start": v(8232.83, 2858.97) * mm, "end": v(8162.83, 2858.97) * mm});
            skLineSegment(sketch, "E65.0.1.50", {"start": v(8788.83, 2859.97) * mm, "end": v(8718.83, 2859.97) * mm});
            skLineSegment(sketch, "E65.0.1.51", {"start": v(9134.83, 2895.97) * mm, "end": v(9066.83, 2859.97) * mm});
            skLineSegment(sketch, "E65.0.1.52", {"start": v(8996.83, 2859.97) * mm, "end": v(8928.83, 2895.97) * mm});
            skLineSegment(sketch, "E65.0.1.53", {"start": v(8232.83, 2859.97) * mm, "end": v(8162.83, 2859.97) * mm});
            skLineSegment(sketch, "E65.0.1.54", {"start": v(8510.83, 2859.97) * mm, "end": v(8440.83, 2859.97) * mm});
            skLineSegment(sketch, "E65.0.1.55", {"start": v(8300.83, 2895.97) * mm, "end": v(8232.83, 2859.97) * mm});
            skLineSegment(sketch, "E65.0.1.56", {"start": v(8578.83, 2895.97) * mm, "end": v(8510.83, 2859.97) * mm});
            skLineSegment(sketch, "E65.0.1.57", {"start": v(8440.83, 2858.97) * mm, "end": v(8372.83, 2894.97) * mm});
            skLineSegment(sketch, "E65.0.2.0", {"start": v(7466.83, 2895.97) * mm, "end": v(7398.83, 2859.97) * mm});
            skLineSegment(sketch, "E65.0.2.1", {"start": v(7466.83, 2894.97) * mm, "end": v(7398.83, 2858.97) * mm});
            skLineSegment(sketch, "E65.0.2.2", {"start": v(7538.83, 2895.97) * mm, "end": v(7466.83, 2895.97) * mm});
            skLineSegment(sketch, "E65.0.2.3", {"start": v(7816.83, 2895.97) * mm, "end": v(7744.83, 2895.97) * mm});
            skLineSegment(sketch, "E65.0.2.4", {"start": v(7606.83, 2858.97) * mm, "end": v(7538.83, 2894.97) * mm});
            skLineSegment(sketch, "E65.0.2.5", {"start": v(7676.83, 2858.97) * mm, "end": v(7606.83, 2858.97) * mm});
            skLineSegment(sketch, "E65.0.2.6", {"start": v(7328.83, 2858.97) * mm, "end": v(7260.83, 2894.97) * mm});
            skLineSegment(sketch, "E65.0.2.7", {"start": v(7744.83, 2894.97) * mm, "end": v(7676.83, 2858.97) * mm});
            skLineSegment(sketch, "E65.0.2.8", {"start": v(7328.83, 2859.97) * mm, "end": v(7260.83, 2895.97) * mm});
            skLineSegment(sketch, "E65.0.2.9", {"start": v(7676.83, 2859.97) * mm, "end": v(7606.83, 2859.97) * mm});
            skLineSegment(sketch, "E65.0.2.10", {"start": v(7954.83, 2858.97) * mm, "end": v(7884.83, 2858.97) * mm});
            skLineSegment(sketch, "E65.0.2.11", {"start": v(7398.83, 2859.97) * mm, "end": v(7328.83, 2859.97) * mm});
            skLineSegment(sketch, "E65.0.2.12", {"start": v(7538.83, 2894.97) * mm, "end": v(7466.83, 2894.97) * mm});
            skLineSegment(sketch, "E65.0.2.13", {"start": v(7884.83, 2858.97) * mm, "end": v(7816.83, 2894.97) * mm});
            skLineSegment(sketch, "E65.0.2.14", {"start": v(7884.83, 2859.97) * mm, "end": v(7816.83, 2895.97) * mm});
            skLineSegment(sketch, "E65.0.2.15", {"start": v(7260.83, 2895.97) * mm, "end": v(7188.83, 2895.97) * mm});
            skLineSegment(sketch, "E65.0.2.16", {"start": v(7744.83, 2895.97) * mm, "end": v(7676.83, 2859.97) * mm});
            skLineSegment(sketch, "E65.0.2.17", {"start": v(7954.83, 2859.97) * mm, "end": v(7884.83, 2859.97) * mm});
            skLineSegment(sketch, "E65.0.2.18", {"start": v(7816.83, 2894.97) * mm, "end": v(7744.83, 2894.97) * mm});
            skLineSegment(sketch, "E65.0.2.19", {"start": v(7606.83, 2859.97) * mm, "end": v(7538.83, 2895.97) * mm});
            skLineSegment(sketch, "E65.0.2.20", {"start": v(7260.83, 2894.97) * mm, "end": v(7188.83, 2894.97) * mm});
            skLineSegment(sketch, "E65.0.2.21", {"start": v(7398.83, 2858.97) * mm, "end": v(7328.83, 2858.97) * mm});
            skLineSegment(sketch, "E65.0.2.22", {"start": v(6494.83, 2859.97) * mm, "end": v(6216.83, 2859.97) * mm, "construction": true});
            skLineSegment(sketch, "E65.0.2.23", {"start": v(6076.83, 2895.97) * mm, "end": v(6008.83, 2859.97) * mm});
            skLineSegment(sketch, "E65.0.2.24", {"start": v(6076.83, 2894.97) * mm, "end": v(6008.83, 2858.97) * mm});
            skLineSegment(sketch, "E65.0.2.25", {"start": v(6494.83, 2858.97) * mm, "end": v(6216.83, 2858.97) * mm, "construction": true});
            skLineSegment(sketch, "E65.0.2.26", {"start": v(6910.83, 2894.97) * mm, "end": v(6842.83, 2858.97) * mm});
            skLineSegment(sketch, "E65.0.2.27", {"start": v(6910.83, 2895.97) * mm, "end": v(6842.83, 2859.97) * mm});
            skLineSegment(sketch, "E65.0.2.28", {"start": v(6148.83, 2895.97) * mm, "end": v(6076.83, 2895.97) * mm});
            skLineSegment(sketch, "E65.0.2.29", {"start": v(6216.83, 2859.97) * mm, "end": v(6148.83, 2895.97) * mm});
            skLineSegment(sketch, "E65.0.2.30", {"start": v(6982.83, 2895.97) * mm, "end": v(6910.83, 2895.97) * mm});
            skLineSegment(sketch, "E65.0.2.31", {"start": v(6982.83, 2894.97) * mm, "end": v(6910.83, 2894.97) * mm});
            skLineSegment(sketch, "E65.0.2.32", {"start": v(6216.83, 2858.97) * mm, "end": v(6148.83, 2894.97) * mm});
            skLineSegment(sketch, "E65.0.2.33", {"start": v(6148.83, 2894.97) * mm, "end": v(6076.83, 2894.97) * mm});
            skLineSegment(sketch, "E65.0.2.34", {"start": v(6564.83, 2858.97) * mm, "end": v(6494.83, 2858.97) * mm});
            skLineSegment(sketch, "E65.0.2.35", {"start": v(6704.83, 2894.97) * mm, "end": v(6632.83, 2894.97) * mm});
            skLineSegment(sketch, "E65.0.2.36", {"start": v(7120.83, 2858.97) * mm, "end": v(7050.83, 2858.97) * mm});
            skLineSegment(sketch, "E65.0.2.37", {"start": v(6354.83, 2894.97) * mm, "end": v(6286.83, 2858.97) * mm});
            skLineSegment(sketch, "E65.0.2.38", {"start": v(6772.83, 2859.97) * mm, "end": v(6704.83, 2895.97) * mm});
            skLineSegment(sketch, "E65.0.2.39", {"start": v(6632.83, 2894.97) * mm, "end": v(6564.83, 2858.97) * mm});
            skLineSegment(sketch, "E65.0.2.40", {"start": v(6426.83, 2895.97) * mm, "end": v(6354.83, 2895.97) * mm});
            skLineSegment(sketch, "E65.0.2.41", {"start": v(6494.83, 2859.97) * mm, "end": v(6426.83, 2895.97) * mm});
            skLineSegment(sketch, "E65.0.2.42", {"start": v(6704.83, 2895.97) * mm, "end": v(6632.83, 2895.97) * mm});
            skLineSegment(sketch, "E65.0.2.43", {"start": v(7120.83, 2859.97) * mm, "end": v(7050.83, 2859.97) * mm});
            skLineSegment(sketch, "E65.0.2.44", {"start": v(6772.83, 2858.97) * mm, "end": v(6704.83, 2894.97) * mm});
            skLineSegment(sketch, "E65.0.2.45", {"start": v(7050.83, 2858.97) * mm, "end": v(6982.83, 2894.97) * mm});
            skLineSegment(sketch, "E65.0.2.46", {"start": v(7188.83, 2894.97) * mm, "end": v(7120.83, 2858.97) * mm});
            skLineSegment(sketch, "E65.0.2.47", {"start": v(6426.83, 2894.97) * mm, "end": v(6354.83, 2894.97) * mm});
            skLineSegment(sketch, "E65.0.2.48", {"start": v(6842.83, 2858.97) * mm, "end": v(6772.83, 2858.97) * mm});
            skLineSegment(sketch, "E65.0.2.49", {"start": v(6286.83, 2858.97) * mm, "end": v(6216.83, 2858.97) * mm});
            skLineSegment(sketch, "E65.0.2.50", {"start": v(6842.83, 2859.97) * mm, "end": v(6772.83, 2859.97) * mm});
            skLineSegment(sketch, "E65.0.2.51", {"start": v(7188.83, 2895.97) * mm, "end": v(7120.83, 2859.97) * mm});
            skLineSegment(sketch, "E65.0.2.52", {"start": v(7050.83, 2859.97) * mm, "end": v(6982.83, 2895.97) * mm});
            skLineSegment(sketch, "E65.0.2.53", {"start": v(6286.83, 2859.97) * mm, "end": v(6216.83, 2859.97) * mm});
            skLineSegment(sketch, "E65.0.2.54", {"start": v(6564.83, 2859.97) * mm, "end": v(6494.83, 2859.97) * mm});
            skLineSegment(sketch, "E65.0.2.55", {"start": v(6354.83, 2895.97) * mm, "end": v(6286.83, 2859.97) * mm});
            skLineSegment(sketch, "E65.0.2.56", {"start": v(6632.83, 2895.97) * mm, "end": v(6564.83, 2859.97) * mm});
            skLineSegment(sketch, "E65.0.2.57", {"start": v(6494.83, 2858.97) * mm, "end": v(6426.83, 2894.97) * mm});
            skLineSegment(sketch, "E65.0.3.0", {"start": v(5520.83, 2895.97) * mm, "end": v(5452.83, 2859.97) * mm});
            skLineSegment(sketch, "E65.0.3.1", {"start": v(5520.83, 2894.97) * mm, "end": v(5452.83, 2858.97) * mm});
            skLineSegment(sketch, "E65.0.3.2", {"start": v(5592.83, 2895.97) * mm, "end": v(5520.83, 2895.97) * mm});
            skLineSegment(sketch, "E65.0.3.3", {"start": v(5870.83, 2895.97) * mm, "end": v(5798.83, 2895.97) * mm});
            skLineSegment(sketch, "E65.0.3.4", {"start": v(5660.83, 2858.97) * mm, "end": v(5592.83, 2894.97) * mm});
            skLineSegment(sketch, "E65.0.3.5", {"start": v(5730.83, 2858.97) * mm, "end": v(5660.83, 2858.97) * mm});
            skLineSegment(sketch, "E65.0.3.6", {"start": v(5382.83, 2858.97) * mm, "end": v(5314.83, 2894.97) * mm});
            skLineSegment(sketch, "E65.0.3.7", {"start": v(5798.83, 2894.97) * mm, "end": v(5730.83, 2858.97) * mm});
            skLineSegment(sketch, "E65.0.3.8", {"start": v(5382.83, 2859.97) * mm, "end": v(5314.83, 2895.97) * mm});
            skLineSegment(sketch, "E65.0.3.9", {"start": v(5730.83, 2859.97) * mm, "end": v(5660.83, 2859.97) * mm});
            skLineSegment(sketch, "E65.0.3.10", {"start": v(6008.83, 2858.97) * mm, "end": v(5938.83, 2858.97) * mm});
            skLineSegment(sketch, "E65.0.3.11", {"start": v(5452.83, 2859.97) * mm, "end": v(5382.83, 2859.97) * mm});
            skLineSegment(sketch, "E65.0.3.12", {"start": v(5592.83, 2894.97) * mm, "end": v(5520.83, 2894.97) * mm});
            skLineSegment(sketch, "E65.0.3.13", {"start": v(5938.83, 2858.97) * mm, "end": v(5870.83, 2894.97) * mm});
            skLineSegment(sketch, "E65.0.3.14", {"start": v(5938.83, 2859.97) * mm, "end": v(5870.83, 2895.97) * mm});
            skLineSegment(sketch, "E65.0.3.15", {"start": v(5314.83, 2895.97) * mm, "end": v(5242.83, 2895.97) * mm});
            skLineSegment(sketch, "E65.0.3.16", {"start": v(5798.83, 2895.97) * mm, "end": v(5730.83, 2859.97) * mm});
            skLineSegment(sketch, "E65.0.3.17", {"start": v(6008.83, 2859.97) * mm, "end": v(5938.83, 2859.97) * mm});
            skLineSegment(sketch, "E65.0.3.18", {"start": v(5870.83, 2894.97) * mm, "end": v(5798.83, 2894.97) * mm});
            skLineSegment(sketch, "E65.0.3.19", {"start": v(5660.83, 2859.97) * mm, "end": v(5592.83, 2895.97) * mm});
            skLineSegment(sketch, "E65.0.3.20", {"start": v(5314.83, 2894.97) * mm, "end": v(5242.83, 2894.97) * mm});
            skLineSegment(sketch, "E65.0.3.21", {"start": v(5452.83, 2858.97) * mm, "end": v(5382.83, 2858.97) * mm});
            skLineSegment(sketch, "E65.0.3.22", {"start": v(4548.83, 2859.97) * mm, "end": v(4270.83, 2859.97) * mm, "construction": true});
            skLineSegment(sketch, "E65.0.3.23", {"start": v(4130.83, 2895.97) * mm, "end": v(4062.83, 2859.97) * mm});
            skLineSegment(sketch, "E65.0.3.24", {"start": v(4130.83, 2894.97) * mm, "end": v(4062.83, 2858.97) * mm});
            skLineSegment(sketch, "E65.0.3.25", {"start": v(4548.83, 2858.97) * mm, "end": v(4270.83, 2858.97) * mm, "construction": true});
            skLineSegment(sketch, "E65.0.3.26", {"start": v(4964.83, 2894.97) * mm, "end": v(4896.83, 2858.97) * mm});
            skLineSegment(sketch, "E65.0.3.27", {"start": v(4964.83, 2895.97) * mm, "end": v(4896.83, 2859.97) * mm});
            skLineSegment(sketch, "E65.0.3.28", {"start": v(4202.83, 2895.97) * mm, "end": v(4130.83, 2895.97) * mm});
            skLineSegment(sketch, "E65.0.3.29", {"start": v(4270.83, 2859.97) * mm, "end": v(4202.83, 2895.97) * mm});
            skLineSegment(sketch, "E65.0.3.30", {"start": v(5036.83, 2895.97) * mm, "end": v(4964.83, 2895.97) * mm});
            skLineSegment(sketch, "E65.0.3.31", {"start": v(5036.83, 2894.97) * mm, "end": v(4964.83, 2894.97) * mm});
            skLineSegment(sketch, "E65.0.3.32", {"start": v(4270.83, 2858.97) * mm, "end": v(4202.83, 2894.97) * mm});
            skLineSegment(sketch, "E65.0.3.33", {"start": v(4202.83, 2894.97) * mm, "end": v(4130.83, 2894.97) * mm});
            skLineSegment(sketch, "E65.0.3.34", {"start": v(4618.83, 2858.97) * mm, "end": v(4548.83, 2858.97) * mm});
            skLineSegment(sketch, "E65.0.3.35", {"start": v(4758.83, 2894.97) * mm, "end": v(4686.83, 2894.97) * mm});
            skLineSegment(sketch, "E65.0.3.36", {"start": v(5174.83, 2858.97) * mm, "end": v(5104.83, 2858.97) * mm});
            skLineSegment(sketch, "E65.0.3.37", {"start": v(4408.83, 2894.97) * mm, "end": v(4340.83, 2858.97) * mm});
            skLineSegment(sketch, "E65.0.3.38", {"start": v(4826.83, 2859.97) * mm, "end": v(4758.83, 2895.97) * mm});
            skLineSegment(sketch, "E65.0.3.39", {"start": v(4686.83, 2894.97) * mm, "end": v(4618.83, 2858.97) * mm});
            skLineSegment(sketch, "E65.0.3.40", {"start": v(4480.83, 2895.97) * mm, "end": v(4408.83, 2895.97) * mm});
            skLineSegment(sketch, "E65.0.3.41", {"start": v(4548.83, 2859.97) * mm, "end": v(4480.83, 2895.97) * mm});
            skLineSegment(sketch, "E65.0.3.42", {"start": v(4758.83, 2895.97) * mm, "end": v(4686.83, 2895.97) * mm});
            skLineSegment(sketch, "E65.0.3.43", {"start": v(5174.83, 2859.97) * mm, "end": v(5104.83, 2859.97) * mm});
            skLineSegment(sketch, "E65.0.3.44", {"start": v(4826.83, 2858.97) * mm, "end": v(4758.83, 2894.97) * mm});
            skLineSegment(sketch, "E65.0.3.45", {"start": v(5104.83, 2858.97) * mm, "end": v(5036.83, 2894.97) * mm});
            skLineSegment(sketch, "E65.0.3.46", {"start": v(5242.83, 2894.97) * mm, "end": v(5174.83, 2858.97) * mm});
            skLineSegment(sketch, "E65.0.3.47", {"start": v(4480.83, 2894.97) * mm, "end": v(4408.83, 2894.97) * mm});
            skLineSegment(sketch, "E65.0.3.48", {"start": v(4896.83, 2858.97) * mm, "end": v(4826.83, 2858.97) * mm});
            skLineSegment(sketch, "E65.0.3.49", {"start": v(4340.83, 2858.97) * mm, "end": v(4270.83, 2858.97) * mm});
            skLineSegment(sketch, "E65.0.3.50", {"start": v(4896.83, 2859.97) * mm, "end": v(4826.83, 2859.97) * mm});
            skLineSegment(sketch, "E65.0.3.51", {"start": v(5242.83, 2895.97) * mm, "end": v(5174.83, 2859.97) * mm});
            skLineSegment(sketch, "E65.0.3.52", {"start": v(5104.83, 2859.97) * mm, "end": v(5036.83, 2895.97) * mm});
            skLineSegment(sketch, "E65.0.3.53", {"start": v(4340.83, 2859.97) * mm, "end": v(4270.83, 2859.97) * mm});
            skLineSegment(sketch, "E65.0.3.54", {"start": v(4618.83, 2859.97) * mm, "end": v(4548.83, 2859.97) * mm});
            skLineSegment(sketch, "E65.0.3.55", {"start": v(4408.83, 2895.97) * mm, "end": v(4340.83, 2859.97) * mm});
            skLineSegment(sketch, "E65.0.3.56", {"start": v(4686.83, 2895.97) * mm, "end": v(4618.83, 2859.97) * mm});
            skLineSegment(sketch, "E65.0.3.57", {"start": v(4548.83, 2858.97) * mm, "end": v(4480.83, 2894.97) * mm});
            skLineSegment(sketch, "E65.0.4.0", {"start": v(3574.83, 2895.97) * mm, "end": v(3506.83, 2859.97) * mm});
            skLineSegment(sketch, "E65.0.4.1", {"start": v(3574.83, 2894.97) * mm, "end": v(3506.83, 2858.97) * mm});
            skLineSegment(sketch, "E65.0.4.2", {"start": v(3646.83, 2895.97) * mm, "end": v(3574.83, 2895.97) * mm});
            skLineSegment(sketch, "E65.0.4.3", {"start": v(3924.83, 2895.97) * mm, "end": v(3852.83, 2895.97) * mm});
            skLineSegment(sketch, "E65.0.4.4", {"start": v(3714.83, 2858.97) * mm, "end": v(3646.83, 2894.97) * mm});
            skLineSegment(sketch, "E65.0.4.5", {"start": v(3784.83, 2858.97) * mm, "end": v(3714.83, 2858.97) * mm});
            skLineSegment(sketch, "E65.0.4.6", {"start": v(3436.83, 2858.97) * mm, "end": v(3368.83, 2894.97) * mm});
            skLineSegment(sketch, "E65.0.4.7", {"start": v(3852.83, 2894.97) * mm, "end": v(3784.83, 2858.97) * mm});
            skLineSegment(sketch, "E65.0.4.8", {"start": v(3436.83, 2859.97) * mm, "end": v(3368.83, 2895.97) * mm});
            skLineSegment(sketch, "E65.0.4.9", {"start": v(3784.83, 2859.97) * mm, "end": v(3714.83, 2859.97) * mm});
            skLineSegment(sketch, "E65.0.4.10", {"start": v(4062.83, 2858.97) * mm, "end": v(3992.83, 2858.97) * mm});
            skLineSegment(sketch, "E65.0.4.11", {"start": v(3506.83, 2859.97) * mm, "end": v(3436.83, 2859.97) * mm});
            skLineSegment(sketch, "E65.0.4.12", {"start": v(3646.83, 2894.97) * mm, "end": v(3574.83, 2894.97) * mm});
            skLineSegment(sketch, "E65.0.4.13", {"start": v(3992.83, 2858.97) * mm, "end": v(3924.83, 2894.97) * mm});
            skLineSegment(sketch, "E65.0.4.14", {"start": v(3992.83, 2859.97) * mm, "end": v(3924.83, 2895.97) * mm});
            skLineSegment(sketch, "E65.0.4.15", {"start": v(3368.83, 2895.97) * mm, "end": v(3296.83, 2895.97) * mm});
            skLineSegment(sketch, "E65.0.4.16", {"start": v(3852.83, 2895.97) * mm, "end": v(3784.83, 2859.97) * mm});
            skLineSegment(sketch, "E65.0.4.17", {"start": v(4062.83, 2859.97) * mm, "end": v(3992.83, 2859.97) * mm});
            skLineSegment(sketch, "E65.0.4.18", {"start": v(3924.83, 2894.97) * mm, "end": v(3852.83, 2894.97) * mm});
            skLineSegment(sketch, "E65.0.4.19", {"start": v(3714.83, 2859.97) * mm, "end": v(3646.83, 2895.97) * mm});
            skLineSegment(sketch, "E65.0.4.20", {"start": v(3368.83, 2894.97) * mm, "end": v(3296.83, 2894.97) * mm});
            skLineSegment(sketch, "E65.0.4.21", {"start": v(3506.83, 2858.97) * mm, "end": v(3436.83, 2858.97) * mm});
            skLineSegment(sketch, "E65.0.4.22", {"start": v(2602.83, 2859.97) * mm, "end": v(2324.83, 2859.97) * mm, "construction": true});
            skLineSegment(sketch, "E65.0.4.23", {"start": v(2184.83, 2895.97) * mm, "end": v(2116.83, 2859.97) * mm});
            skLineSegment(sketch, "E65.0.4.24", {"start": v(2184.83, 2894.97) * mm, "end": v(2116.83, 2858.97) * mm});
            skLineSegment(sketch, "E65.0.4.25", {"start": v(2602.83, 2858.97) * mm, "end": v(2324.83, 2858.97) * mm, "construction": true});
            skLineSegment(sketch, "E65.0.4.26", {"start": v(3018.83, 2894.97) * mm, "end": v(2950.83, 2858.97) * mm});
            skLineSegment(sketch, "E65.0.4.27", {"start": v(3018.83, 2895.97) * mm, "end": v(2950.83, 2859.97) * mm});
            skLineSegment(sketch, "E65.0.4.28", {"start": v(2256.83, 2895.97) * mm, "end": v(2184.83, 2895.97) * mm});
            skLineSegment(sketch, "E65.0.4.29", {"start": v(2324.83, 2859.97) * mm, "end": v(2256.83, 2895.97) * mm});
            skLineSegment(sketch, "E65.0.4.30", {"start": v(3090.83, 2895.97) * mm, "end": v(3018.83, 2895.97) * mm});
            skLineSegment(sketch, "E65.0.4.31", {"start": v(3090.83, 2894.97) * mm, "end": v(3018.83, 2894.97) * mm});
            skLineSegment(sketch, "E65.0.4.32", {"start": v(2324.83, 2858.97) * mm, "end": v(2256.83, 2894.97) * mm});
            skLineSegment(sketch, "E65.0.4.33", {"start": v(2256.83, 2894.97) * mm, "end": v(2184.83, 2894.97) * mm});
            skLineSegment(sketch, "E65.0.4.34", {"start": v(2672.83, 2858.97) * mm, "end": v(2602.83, 2858.97) * mm});
            skLineSegment(sketch, "E65.0.4.35", {"start": v(2812.83, 2894.97) * mm, "end": v(2740.83, 2894.97) * mm});
            skLineSegment(sketch, "E65.0.4.36", {"start": v(3228.83, 2858.97) * mm, "end": v(3158.83, 2858.97) * mm});
            skLineSegment(sketch, "E65.0.4.37", {"start": v(2462.83, 2894.97) * mm, "end": v(2394.83, 2858.97) * mm});
            skLineSegment(sketch, "E65.0.4.38", {"start": v(2880.83, 2859.97) * mm, "end": v(2812.83, 2895.97) * mm});
            skLineSegment(sketch, "E65.0.4.39", {"start": v(2740.83, 2894.97) * mm, "end": v(2672.83, 2858.97) * mm});
            skLineSegment(sketch, "E65.0.4.40", {"start": v(2534.83, 2895.97) * mm, "end": v(2462.83, 2895.97) * mm});
            skLineSegment(sketch, "E65.0.4.41", {"start": v(2602.83, 2859.97) * mm, "end": v(2534.83, 2895.97) * mm});
            skLineSegment(sketch, "E65.0.4.42", {"start": v(2812.83, 2895.97) * mm, "end": v(2740.83, 2895.97) * mm});
            skLineSegment(sketch, "E65.0.4.43", {"start": v(3228.83, 2859.97) * mm, "end": v(3158.83, 2859.97) * mm});
            skLineSegment(sketch, "E65.0.4.44", {"start": v(2880.83, 2858.97) * mm, "end": v(2812.83, 2894.97) * mm});
            skLineSegment(sketch, "E65.0.4.45", {"start": v(3158.83, 2858.97) * mm, "end": v(3090.83, 2894.97) * mm});
            skLineSegment(sketch, "E65.0.4.46", {"start": v(3296.83, 2894.97) * mm, "end": v(3228.83, 2858.97) * mm});
            skLineSegment(sketch, "E65.0.4.47", {"start": v(2534.83, 2894.97) * mm, "end": v(2462.83, 2894.97) * mm});
            skLineSegment(sketch, "E65.0.4.48", {"start": v(2950.83, 2858.97) * mm, "end": v(2880.83, 2858.97) * mm});
            skLineSegment(sketch, "E65.0.4.49", {"start": v(2394.83, 2858.97) * mm, "end": v(2324.83, 2858.97) * mm});
            skLineSegment(sketch, "E65.0.4.50", {"start": v(2950.83, 2859.97) * mm, "end": v(2880.83, 2859.97) * mm});
            skLineSegment(sketch, "E65.0.4.51", {"start": v(3296.83, 2895.97) * mm, "end": v(3228.83, 2859.97) * mm});
            skLineSegment(sketch, "E65.0.4.52", {"start": v(3158.83, 2859.97) * mm, "end": v(3090.83, 2895.97) * mm});
            skLineSegment(sketch, "E65.0.4.53", {"start": v(2394.83, 2859.97) * mm, "end": v(2324.83, 2859.97) * mm});
            skLineSegment(sketch, "E65.0.4.54", {"start": v(2672.83, 2859.97) * mm, "end": v(2602.83, 2859.97) * mm});
            skLineSegment(sketch, "E65.0.4.55", {"start": v(2462.83, 2895.97) * mm, "end": v(2394.83, 2859.97) * mm});
            skLineSegment(sketch, "E65.0.4.56", {"start": v(2740.83, 2895.97) * mm, "end": v(2672.83, 2859.97) * mm});
            skLineSegment(sketch, "E65.0.4.57", {"start": v(2602.83, 2858.97) * mm, "end": v(2534.83, 2894.97) * mm});
            skLineSegment(sketch, "E65.0.5.0", {"start": v(1628.83, 2895.97) * mm, "end": v(1560.83, 2859.97) * mm});
            skLineSegment(sketch, "E65.0.5.1", {"start": v(1628.83, 2894.97) * mm, "end": v(1560.83, 2858.97) * mm});
            skLineSegment(sketch, "E65.0.5.2", {"start": v(1700.83, 2895.97) * mm, "end": v(1628.83, 2895.97) * mm});
            skLineSegment(sketch, "E65.0.5.3", {"start": v(1978.83, 2895.97) * mm, "end": v(1906.83, 2895.97) * mm});
            skLineSegment(sketch, "E65.0.5.4", {"start": v(1768.83, 2858.97) * mm, "end": v(1700.83, 2894.97) * mm});
            skLineSegment(sketch, "E65.0.5.5", {"start": v(1838.83, 2858.97) * mm, "end": v(1768.83, 2858.97) * mm});
            skLineSegment(sketch, "E65.0.5.6", {"start": v(1490.83, 2858.97) * mm, "end": v(1422.83, 2894.97) * mm});
            skLineSegment(sketch, "E65.0.5.7", {"start": v(1906.83, 2894.97) * mm, "end": v(1838.83, 2858.97) * mm});
            skLineSegment(sketch, "E65.0.5.8", {"start": v(1490.83, 2859.97) * mm, "end": v(1422.83, 2895.97) * mm});
            skLineSegment(sketch, "E65.0.5.9", {"start": v(1838.83, 2859.97) * mm, "end": v(1768.83, 2859.97) * mm});
            skLineSegment(sketch, "E65.0.5.10", {"start": v(2116.83, 2858.97) * mm, "end": v(2046.83, 2858.97) * mm});
            skLineSegment(sketch, "E65.0.5.11", {"start": v(1560.83, 2859.97) * mm, "end": v(1490.83, 2859.97) * mm});
            skLineSegment(sketch, "E65.0.5.12", {"start": v(1700.83, 2894.97) * mm, "end": v(1628.83, 2894.97) * mm});
            skLineSegment(sketch, "E65.0.5.13", {"start": v(2046.83, 2858.97) * mm, "end": v(1978.83, 2894.97) * mm});
            skLineSegment(sketch, "E65.0.5.14", {"start": v(2046.83, 2859.97) * mm, "end": v(1978.83, 2895.97) * mm});
            skLineSegment(sketch, "E65.0.5.15", {"start": v(1422.83, 2895.97) * mm, "end": v(1350.83, 2895.97) * mm});
            skLineSegment(sketch, "E65.0.5.16", {"start": v(1906.83, 2895.97) * mm, "end": v(1838.83, 2859.97) * mm});
            skLineSegment(sketch, "E65.0.5.17", {"start": v(2116.83, 2859.97) * mm, "end": v(2046.83, 2859.97) * mm});
            skLineSegment(sketch, "E65.0.5.18", {"start": v(1978.83, 2894.97) * mm, "end": v(1906.83, 2894.97) * mm});
            skLineSegment(sketch, "E65.0.5.19", {"start": v(1768.83, 2859.97) * mm, "end": v(1700.83, 2895.97) * mm});
            skLineSegment(sketch, "E65.0.5.20", {"start": v(1422.83, 2894.97) * mm, "end": v(1350.83, 2894.97) * mm});
            skLineSegment(sketch, "E65.0.5.21", {"start": v(1560.83, 2858.97) * mm, "end": v(1490.83, 2858.97) * mm});
            skLineSegment(sketch, "E65.0.5.22", {"start": v(656.83, 2859.97) * mm, "end": v(378.83, 2859.97) * mm, "construction": true});
            skLineSegment(sketch, "E65.0.5.23", {"start": v(238.83, 2895.97) * mm, "end": v(170.83, 2859.97) * mm});
            skLineSegment(sketch, "E65.0.5.24", {"start": v(238.83, 2894.97) * mm, "end": v(170.83, 2858.97) * mm});
            skLineSegment(sketch, "E65.0.5.25", {"start": v(656.83, 2858.97) * mm, "end": v(378.83, 2858.97) * mm, "construction": true});
            skLineSegment(sketch, "E65.0.5.26", {"start": v(1072.83, 2894.97) * mm, "end": v(1004.83, 2858.97) * mm});
            skLineSegment(sketch, "E65.0.5.27", {"start": v(1072.83, 2895.97) * mm, "end": v(1004.83, 2859.97) * mm});
            skLineSegment(sketch, "E65.0.5.28", {"start": v(310.83, 2895.97) * mm, "end": v(238.83, 2895.97) * mm});
            skLineSegment(sketch, "E65.0.5.29", {"start": v(378.83, 2859.97) * mm, "end": v(310.83, 2895.97) * mm});
            skLineSegment(sketch, "E65.0.5.30", {"start": v(1144.83, 2895.97) * mm, "end": v(1072.83, 2895.97) * mm});
            skLineSegment(sketch, "E65.0.5.31", {"start": v(1144.83, 2894.97) * mm, "end": v(1072.83, 2894.97) * mm});
            skLineSegment(sketch, "E65.0.5.32", {"start": v(378.83, 2858.97) * mm, "end": v(310.83, 2894.97) * mm});
            skLineSegment(sketch, "E65.0.5.33", {"start": v(310.83, 2894.97) * mm, "end": v(238.83, 2894.97) * mm});
            skLineSegment(sketch, "E65.0.5.34", {"start": v(726.83, 2858.97) * mm, "end": v(656.83, 2858.97) * mm});
            skLineSegment(sketch, "E65.0.5.35", {"start": v(866.83, 2894.97) * mm, "end": v(794.83, 2894.97) * mm});
            skLineSegment(sketch, "E65.0.5.36", {"start": v(1282.83, 2858.97) * mm, "end": v(1212.83, 2858.97) * mm});
            skLineSegment(sketch, "E65.0.5.37", {"start": v(516.83, 2894.97) * mm, "end": v(448.83, 2858.97) * mm});
            skLineSegment(sketch, "E65.0.5.38", {"start": v(934.83, 2859.97) * mm, "end": v(866.83, 2895.97) * mm});
            skLineSegment(sketch, "E65.0.5.39", {"start": v(794.83, 2894.97) * mm, "end": v(726.83, 2858.97) * mm});
            skLineSegment(sketch, "E65.0.5.40", {"start": v(588.83, 2895.97) * mm, "end": v(516.83, 2895.97) * mm});
            skLineSegment(sketch, "E65.0.5.41", {"start": v(656.83, 2859.97) * mm, "end": v(588.83, 2895.97) * mm});
            skLineSegment(sketch, "E65.0.5.42", {"start": v(866.83, 2895.97) * mm, "end": v(794.83, 2895.97) * mm});
            skLineSegment(sketch, "E65.0.5.43", {"start": v(1282.83, 2859.97) * mm, "end": v(1212.83, 2859.97) * mm});
            skLineSegment(sketch, "E65.0.5.44", {"start": v(934.83, 2858.97) * mm, "end": v(866.83, 2894.97) * mm});
            skLineSegment(sketch, "E65.0.5.45", {"start": v(1212.83, 2858.97) * mm, "end": v(1144.83, 2894.97) * mm});
            skLineSegment(sketch, "E65.0.5.46", {"start": v(1350.83, 2894.97) * mm, "end": v(1282.83, 2858.97) * mm});
            skLineSegment(sketch, "E65.0.5.47", {"start": v(588.83, 2894.97) * mm, "end": v(516.83, 2894.97) * mm});
            skLineSegment(sketch, "E65.0.5.48", {"start": v(1004.83, 2858.97) * mm, "end": v(934.83, 2858.97) * mm});
            skLineSegment(sketch, "E65.0.5.49", {"start": v(448.83, 2858.97) * mm, "end": v(378.83, 2858.97) * mm});
            skLineSegment(sketch, "E65.0.5.50", {"start": v(1004.83, 2859.97) * mm, "end": v(934.83, 2859.97) * mm});
            skLineSegment(sketch, "E65.0.5.51", {"start": v(1350.83, 2895.97) * mm, "end": v(1282.83, 2859.97) * mm});
            skLineSegment(sketch, "E65.0.5.52", {"start": v(1212.83, 2859.97) * mm, "end": v(1144.83, 2895.97) * mm});
            skLineSegment(sketch, "E65.0.5.53", {"start": v(448.83, 2859.97) * mm, "end": v(378.83, 2859.97) * mm});
            skLineSegment(sketch, "E65.0.5.54", {"start": v(726.83, 2859.97) * mm, "end": v(656.83, 2859.97) * mm});
            skLineSegment(sketch, "E65.0.5.55", {"start": v(516.83, 2895.97) * mm, "end": v(448.83, 2859.97) * mm});
            skLineSegment(sketch, "E65.0.5.56", {"start": v(794.83, 2895.97) * mm, "end": v(726.83, 2859.97) * mm});
            skLineSegment(sketch, "E65.0.5.57", {"start": v(656.83, 2858.97) * mm, "end": v(588.83, 2894.97) * mm});
            skLineSegment(sketch, "E65.direction1", {"start": v(11846.83, 2858.97) * mm, "end": v(11846.83, 2883.97) * mm, "construction": true});
            skLineSegment(sketch, "E65.direction2", {"start": v(11846.83, 2858.97) * mm, "end": v(9900.83, 2858.97) * mm, "construction": true});
            skLineSegment(sketch, "E66", {"start": v(170.83, 2859.97) * mm, "end": v(100, 2859.97) * mm});
            skLineSegment(sketch, "E67", {"start": v(100, 2859.97) * mm, "end": v(100, 2858.97) * mm});
            skLineSegment(sketch, "E68", {"start": v(100, 2858.97) * mm, "end": v(170.83, 2858.97) * mm});
            skSolve(sketch);
        }
        {
            var Q0;
            Q0=qSketchRegion(id+"F14",true);
            extrude(context, id + "F15", {"entities" : qUnion([Q0]), "operationType" : NewBodyOperationType.ADD, "depth" : 2236 * mm, "offsetDistance" : 25 * mm});
        }
    });
